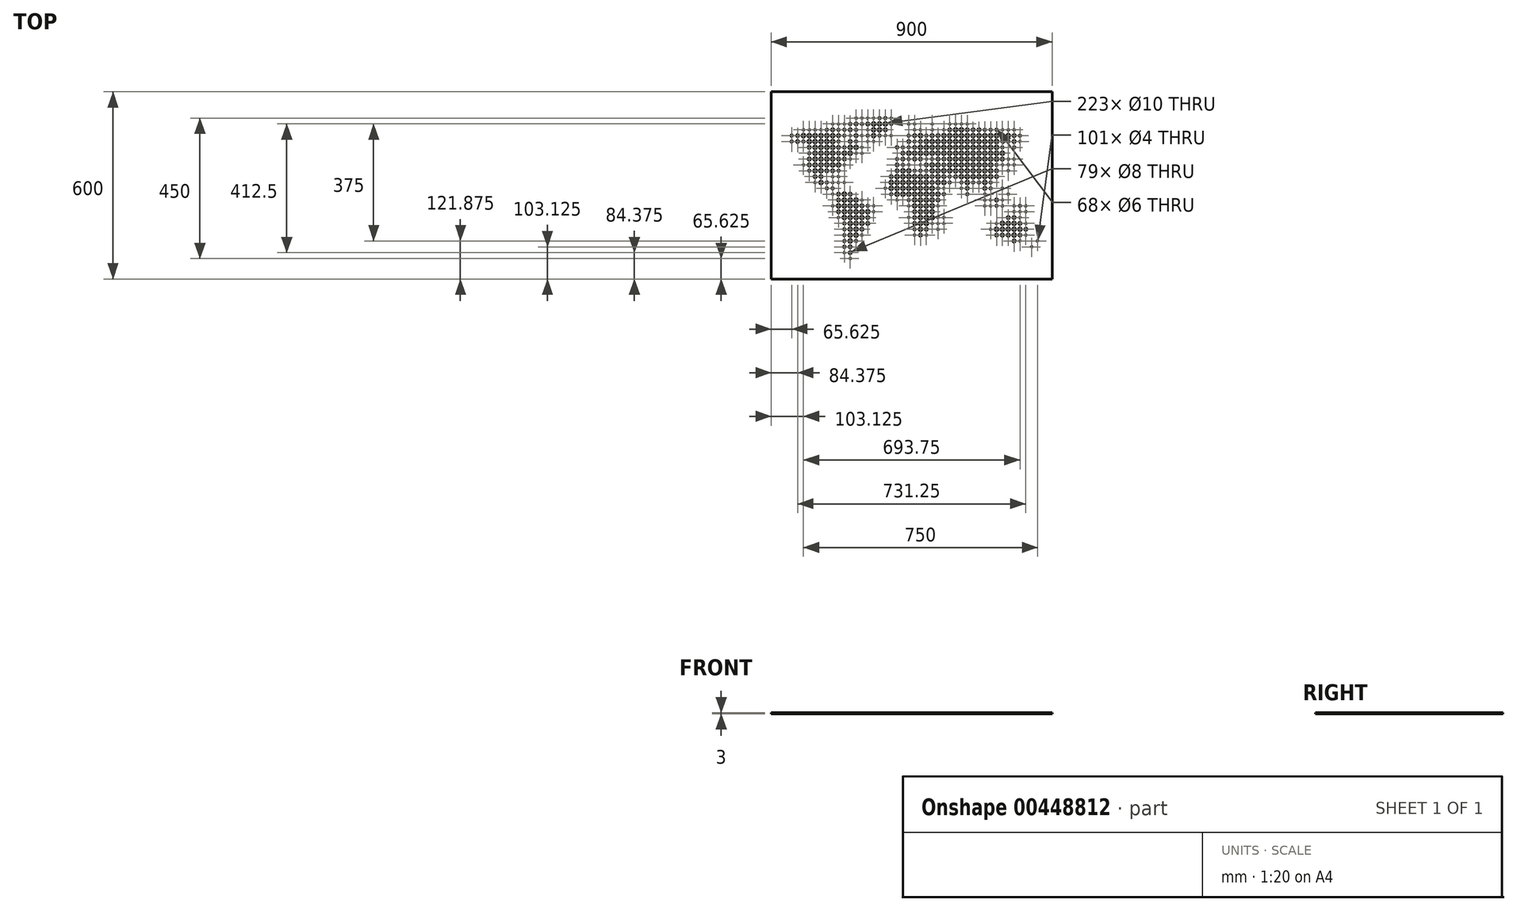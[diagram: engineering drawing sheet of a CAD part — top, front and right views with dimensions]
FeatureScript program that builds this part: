
annotation { "Feature Type Name" : "Feature", "Feature Type Description" : "" }
export const myFeature = defineFeature(function(context is Context, id is Id, definition is map)
    precondition{}
    {
        {
            var Q0;
            Q0=qCreatedBy(makeId("Top.planeOp"),FACE);
            var sketch = newSketch(context, id + "F0", { "sketchPlane" : qUnion([Q0])});
            skLineSegment(sketch, "E0.bottom", {"start": v(450, -300) * mm, "end": v(-450, -300) * mm});
            skLineSegment(sketch, "E0.top", {"start": v(450, 300) * mm, "end": v(-450, 300) * mm});
            skLineSegment(sketch, "E0.left", {"start": v(450, -300) * mm, "end": v(450, 300) * mm});
            skLineSegment(sketch, "E0.right", {"start": v(-450, -300) * mm, "end": v(-450, 300) * mm});
            skPoint(sketch, "E0.middle", {"position": v(0, 0) * mm});
            skSolve(sketch);
        }
        {
            var Q0;
            Q0=makeQuery(id+"F0.imprint","IMPRINT",FACE,{"disambiguationData":[TD([[makeQuery(id+"F0.imprint","IMPRINT",EDGE,{"derivedFrom":sQuery(id+"F0.wireOp",EDGE,"E0.bottom")}),-1.0]])]});
            extrude(context, id + "F1", {"entities" : qUnion([Q0]), "depth" : 3 * mm});
        }
        {
            var Q0;
            Q0=makeQuery(id+"F1.opExtrude","CAP_FACE",FACE,{"disambiguationData":[OSD([sQuery(id+"F0.wireOp",EDGE,"E0.bottom"),sQuery(id+"F0.wireOp",EDGE,"E0.top"),sQuery(id+"F0.wireOp",EDGE,"E0.left"),sQuery(id+"F0.wireOp",EDGE,"E0.right")])],"isStart":false});
            var sketch = newSketch(context, id + "F2", { "sketchPlane" : qUnion([Q0])});
            skLineSegment(sketch, "E1", {"start": v(-440.63, 300) * mm, "end": v(-440.62, -300) * mm, "construction": true});
            skLineSegment(sketch, "E2.1.0.0", {"start": v(-421.88, 300) * mm, "end": v(-421.88, -300) * mm, "construction": true});
            skLineSegment(sketch, "E2.2.0.0", {"start": v(-403.13, 300) * mm, "end": v(-403.13, -300) * mm, "construction": true});
            skLineSegment(sketch, "E2.3.0.0", {"start": v(-384.38, 300) * mm, "end": v(-384.38, -300) * mm, "construction": true});
            skLineSegment(sketch, "E2.4.0.0", {"start": v(-365.63, 300) * mm, "end": v(-365.63, -300) * mm, "construction": true});
            skLineSegment(sketch, "E2.5.0.0", {"start": v(-346.88, 300) * mm, "end": v(-346.88, -300) * mm, "construction": true});
            skLineSegment(sketch, "E2.6.0.0", {"start": v(-328.13, 300) * mm, "end": v(-328.13, -300) * mm, "construction": true});
            skLineSegment(sketch, "E2.7.0.0", {"start": v(-309.38, 300) * mm, "end": v(-309.38, -300) * mm, "construction": true});
            skLineSegment(sketch, "E2.8.0.0", {"start": v(-290.63, 300) * mm, "end": v(-290.63, -300) * mm, "construction": true});
            skLineSegment(sketch, "E2.9.0.0", {"start": v(-271.88, 300) * mm, "end": v(-271.88, -300) * mm, "construction": true});
            skLineSegment(sketch, "E2.direction1", {"start": v(-440.62, -300) * mm, "end": v(-421.88, -300) * mm, "construction": true});
            skLineSegment(sketch, "E3.0.10.0", {"start": v(-253.13, 300) * mm, "end": v(-253.13, -300) * mm, "construction": true});
            skLineSegment(sketch, "E3.0.11.0", {"start": v(-234.38, 300) * mm, "end": v(-234.38, -300) * mm, "construction": true});
            skLineSegment(sketch, "E3.0.12.0", {"start": v(-215.63, 300) * mm, "end": v(-215.63, -300) * mm, "construction": true});
            skLineSegment(sketch, "E3.0.13.0", {"start": v(-196.88, 300) * mm, "end": v(-196.88, -300) * mm, "construction": true});
            skLineSegment(sketch, "E3.0.14.0", {"start": v(-178.13, 300) * mm, "end": v(-178.13, -300) * mm, "construction": true});
            skLineSegment(sketch, "E3.0.15.0", {"start": v(-159.38, 300) * mm, "end": v(-159.38, -300) * mm, "construction": true});
            skLineSegment(sketch, "E3.0.16.0", {"start": v(-140.63, 300) * mm, "end": v(-140.63, -300) * mm, "construction": true});
            skLineSegment(sketch, "E3.0.17.0", {"start": v(-121.88, 300) * mm, "end": v(-121.88, -300) * mm, "construction": true});
            skLineSegment(sketch, "E3.0.18.0", {"start": v(-103.13, 300) * mm, "end": v(-103.13, -300) * mm, "construction": true});
            skLineSegment(sketch, "E3.0.19.0", {"start": v(-84.38, 300) * mm, "end": v(-84.38, -300) * mm, "construction": true});
            skLineSegment(sketch, "E4.0.20.0", {"start": v(-65.63, 300) * mm, "end": v(-65.63, -300) * mm, "construction": true});
            skLineSegment(sketch, "E4.0.21.0", {"start": v(-46.88, 300) * mm, "end": v(-46.88, -300) * mm, "construction": true});
            skLineSegment(sketch, "E4.0.22.0", {"start": v(-28.13, 300) * mm, "end": v(-28.13, -300) * mm, "construction": true});
            skLineSegment(sketch, "E4.0.23.0", {"start": v(-9.38, 300) * mm, "end": v(-9.38, -300) * mm, "construction": true});
            skLineSegment(sketch, "E4.0.24.0", {"start": v(9.37, 300) * mm, "end": v(9.37, -300) * mm, "construction": true});
            skLineSegment(sketch, "E4.0.25.0", {"start": v(28.12, 300) * mm, "end": v(28.12, -300) * mm, "construction": true});
            skLineSegment(sketch, "E4.0.26.0", {"start": v(46.87, 300) * mm, "end": v(46.87, -300) * mm, "construction": true});
            skLineSegment(sketch, "E4.0.27.0", {"start": v(65.62, 300) * mm, "end": v(65.62, -300) * mm, "construction": true});
            skLineSegment(sketch, "E4.0.28.0", {"start": v(84.37, 300) * mm, "end": v(84.37, -300) * mm, "construction": true});
            skLineSegment(sketch, "E4.0.29.0", {"start": v(103.12, 300) * mm, "end": v(103.12, -300) * mm, "construction": true});
            skLineSegment(sketch, "E5.0.30.0", {"start": v(121.87, 300) * mm, "end": v(121.87, -300) * mm, "construction": true});
            skLineSegment(sketch, "E5.0.31.0", {"start": v(140.62, 300) * mm, "end": v(140.62, -300) * mm, "construction": true});
            skLineSegment(sketch, "E5.0.32.0", {"start": v(159.37, 300) * mm, "end": v(159.37, -300) * mm, "construction": true});
            skLineSegment(sketch, "E5.0.33.0", {"start": v(178.12, 300) * mm, "end": v(178.12, -300) * mm, "construction": true});
            skLineSegment(sketch, "E5.0.34.0", {"start": v(196.87, 300) * mm, "end": v(196.87, -300) * mm, "construction": true});
            skLineSegment(sketch, "E5.0.35.0", {"start": v(215.62, 300) * mm, "end": v(215.62, -300) * mm, "construction": true});
            skLineSegment(sketch, "E5.0.36.0", {"start": v(234.37, 300) * mm, "end": v(234.37, -300) * mm, "construction": true});
            skLineSegment(sketch, "E5.0.37.0", {"start": v(253.12, 300) * mm, "end": v(253.12, -300) * mm, "construction": true});
            skLineSegment(sketch, "E5.0.38.0", {"start": v(271.87, 300) * mm, "end": v(271.87, -300) * mm, "construction": true});
            skLineSegment(sketch, "E5.0.39.0", {"start": v(290.62, 300) * mm, "end": v(290.62, -300) * mm, "construction": true});
            skLineSegment(sketch, "E5.0.40.0", {"start": v(309.37, 300) * mm, "end": v(309.37, -300) * mm, "construction": true});
            skLineSegment(sketch, "E5.0.41.0", {"start": v(328.12, 300) * mm, "end": v(328.12, -300) * mm, "construction": true});
            skLineSegment(sketch, "E5.0.42.0", {"start": v(346.87, 300) * mm, "end": v(346.87, -300) * mm, "construction": true});
            skLineSegment(sketch, "E5.0.43.0", {"start": v(365.62, 300) * mm, "end": v(365.62, -300) * mm, "construction": true});
            skLineSegment(sketch, "E5.0.44.0", {"start": v(384.37, 300) * mm, "end": v(384.37, -300) * mm, "construction": true});
            skLineSegment(sketch, "E5.0.45.0", {"start": v(403.12, 300) * mm, "end": v(403.12, -300) * mm, "construction": true});
            skLineSegment(sketch, "E5.0.46.0", {"start": v(421.87, 300) * mm, "end": v(421.87, -300) * mm, "construction": true});
            skLineSegment(sketch, "E5.0.47.0", {"start": v(440.62, 300) * mm, "end": v(440.62, -300) * mm, "construction": true});
            skLineSegment(sketch, "E6", {"start": v(-450, -290.63) * mm, "end": v(450, -290.63) * mm, "construction": true});
            skLineSegment(sketch, "E7.0.1.0", {"start": v(-450, -271.88) * mm, "end": v(450, -271.88) * mm, "construction": true});
            skLineSegment(sketch, "E7.0.2.0", {"start": v(-450, -253.13) * mm, "end": v(450, -253.13) * mm, "construction": true});
            skLineSegment(sketch, "E7.0.3.0", {"start": v(-450, -234.38) * mm, "end": v(450, -234.38) * mm, "construction": true});
            skLineSegment(sketch, "E7.0.4.0", {"start": v(-450, -215.63) * mm, "end": v(450, -215.63) * mm, "construction": true});
            skLineSegment(sketch, "E7.0.5.0", {"start": v(-450, -196.88) * mm, "end": v(450, -196.88) * mm, "construction": true});
            skLineSegment(sketch, "E7.0.6.0", {"start": v(-450, -178.13) * mm, "end": v(450, -178.13) * mm, "construction": true});
            skLineSegment(sketch, "E7.0.7.0", {"start": v(-450, -159.38) * mm, "end": v(450, -159.38) * mm, "construction": true});
            skLineSegment(sketch, "E7.0.8.0", {"start": v(-450, -140.63) * mm, "end": v(450, -140.63) * mm, "construction": true});
            skLineSegment(sketch, "E7.0.9.0", {"start": v(-450, -121.88) * mm, "end": v(450, -121.88) * mm, "construction": true});
            skLineSegment(sketch, "E7.direction1", {"start": v(-450, -290.63) * mm, "end": v(-425, -290.63) * mm, "construction": true});
            skLineSegment(sketch, "E7.direction2", {"start": v(-450, -290.63) * mm, "end": v(-450, -271.88) * mm, "construction": true});
            skLineSegment(sketch, "E8.0.0.10", {"start": v(-450, -103.13) * mm, "end": v(450, -103.13) * mm, "construction": true});
            skLineSegment(sketch, "E8.0.0.11", {"start": v(-450, -84.38) * mm, "end": v(450, -84.38) * mm, "construction": true});
            skLineSegment(sketch, "E8.0.0.12", {"start": v(-450, -65.63) * mm, "end": v(450, -65.63) * mm, "construction": true});
            skLineSegment(sketch, "E8.0.0.13", {"start": v(-450, -46.88) * mm, "end": v(450, -46.88) * mm, "construction": true});
            skLineSegment(sketch, "E8.0.0.14", {"start": v(-450, -28.13) * mm, "end": v(450, -28.13) * mm, "construction": true});
            skLineSegment(sketch, "E8.0.0.15", {"start": v(-450, -9.38) * mm, "end": v(450, -9.38) * mm, "construction": true});
            skLineSegment(sketch, "E8.0.0.16", {"start": v(-450, 9.37) * mm, "end": v(450, 9.37) * mm, "construction": true});
            skLineSegment(sketch, "E8.0.0.17", {"start": v(-450, 28.12) * mm, "end": v(450, 28.12) * mm, "construction": true});
            skLineSegment(sketch, "E8.0.0.18", {"start": v(-450, 46.87) * mm, "end": v(450, 46.87) * mm, "construction": true});
            skLineSegment(sketch, "E8.0.0.19", {"start": v(-450, 65.62) * mm, "end": v(450, 65.62) * mm, "construction": true});
            skLineSegment(sketch, "E9.0.0.20", {"start": v(-450, 84.37) * mm, "end": v(450, 84.37) * mm, "construction": true});
            skLineSegment(sketch, "E9.0.0.21", {"start": v(-450, 103.12) * mm, "end": v(450, 103.12) * mm, "construction": true});
            skLineSegment(sketch, "E9.0.0.22", {"start": v(-450, 121.87) * mm, "end": v(450, 121.87) * mm, "construction": true});
            skLineSegment(sketch, "E9.0.0.23", {"start": v(-450, 140.62) * mm, "end": v(450, 140.62) * mm, "construction": true});
            skLineSegment(sketch, "E9.0.0.24", {"start": v(-450, 159.37) * mm, "end": v(450, 159.37) * mm, "construction": true});
            skLineSegment(sketch, "E9.0.0.25", {"start": v(-450, 178.12) * mm, "end": v(450, 178.12) * mm, "construction": true});
            skLineSegment(sketch, "E9.0.0.26", {"start": v(-450, 196.87) * mm, "end": v(450, 196.87) * mm, "construction": true});
            skLineSegment(sketch, "E9.0.0.27", {"start": v(-450, 215.62) * mm, "end": v(450, 215.62) * mm, "construction": true});
            skLineSegment(sketch, "E9.0.0.28", {"start": v(-450, 234.37) * mm, "end": v(450, 234.37) * mm, "construction": true});
            skLineSegment(sketch, "E9.0.0.29", {"start": v(-450, 253.12) * mm, "end": v(450, 253.12) * mm, "construction": true});
            skLineSegment(sketch, "E10.0.0.30", {"start": v(-450, 271.87) * mm, "end": v(450, 271.87) * mm, "construction": true});
            skLineSegment(sketch, "E10.0.0.31", {"start": v(-450, 290.62) * mm, "end": v(450, 290.62) * mm, "construction": true});
            skSolve(sketch);
        }
        {
            var Q0;
            Q0=makeQuery(id+"F2.imprint","IMPRINT",FACE,{"disambiguationData":[TD([[makeQuery(id+"F2.imprint","IMPRINT",EDGE,{"derivedFrom":makeQuery(id+"F1.opExtrude","CAP_EDGE",EDGE,{"disambiguationData":[OSD([sQuery(id+"F0.wireOp",EDGE,"E0.bottom")])],"isStart":false})}),-1.0]])]});
            var sketch = newSketch(context, id + "F3", { "sketchPlane" : qUnion([Q0])});
            skPoint(sketch, "E11", {"position": v(-65.63, 215.62) * mm});
            skPoint(sketch, "E12", {"position": v(-121.88, 215.62) * mm});
            skPoint(sketch, "E13", {"position": v(-140.63, 215.62) * mm});
            skPoint(sketch, "E14", {"position": v(-159.38, 215.62) * mm});
            skPoint(sketch, "E15", {"position": v(-178.13, 215.62) * mm});
            skPoint(sketch, "E16", {"position": v(-215.63, 196.87) * mm});
            skPoint(sketch, "E17", {"position": v(-234.38, 196.87) * mm});
            skPoint(sketch, "E18", {"position": v(-253.13, 196.87) * mm});
            skPoint(sketch, "E19", {"position": v(-290.63, 178.12) * mm});
            skPoint(sketch, "E20", {"position": v(-309.38, 178.12) * mm});
            skPoint(sketch, "E21", {"position": v(-328.13, 178.12) * mm});
            skPoint(sketch, "E22", {"position": v(-346.88, 178.12) * mm});
            skPoint(sketch, "E23", {"position": v(-140.63, 178.12) * mm});
            skPoint(sketch, "E24", {"position": v(-65.63, 159.37) * mm});
            skPoint(sketch, "E25", {"position": v(-84.38, 159.37) * mm});
            skPoint(sketch, "E26", {"position": v(-140.63, 140.62) * mm});
            skPoint(sketch, "E27", {"position": v(-121.88, 140.62) * mm});
            skPoint(sketch, "E28", {"position": v(-159.38, 121.87) * mm});
            skPoint(sketch, "E29", {"position": v(-159.38, 103.12) * mm});
            skPoint(sketch, "E30", {"position": v(-178.13, 103.12) * mm});
            skPoint(sketch, "E31", {"position": v(-196.88, 84.37) * mm});
            skPoint(sketch, "E32", {"position": v(-215.63, 65.62) * mm});
            skPoint(sketch, "E33", {"position": v(-234.38, 28.12) * mm});
            skPoint(sketch, "E34", {"position": v(-253.13, 28.12) * mm});
            skPoint(sketch, "E35", {"position": v(-253.13, 9.37) * mm});
            skPoint(sketch, "E36", {"position": v(-234.38, 9.37) * mm});
            skPoint(sketch, "E37", {"position": v(-215.63, 9.37) * mm});
            skPoint(sketch, "E38", {"position": v(-309.38, 9.37) * mm});
            skPoint(sketch, "E39", {"position": v(-253.13, -28.13) * mm});
            skPoint(sketch, "E40", {"position": v(-253.13, -65.63) * mm});
            skPoint(sketch, "E41", {"position": v(-159.38, -46.88) * mm});
            skPoint(sketch, "E42", {"position": v(-121.88, -65.63) * mm});
            skPoint(sketch, "E43", {"position": v(-121.88, -84.38) * mm});
            skPoint(sketch, "E44", {"position": v(-234.38, -103.13) * mm});
            skPoint(sketch, "E45", {"position": v(-215.63, -215.63) * mm});
            skPoint(sketch, "E46", {"position": v(-196.88, -234.38) * mm});
            skPoint(sketch, "E47", {"position": v(-159.38, -159.38) * mm});
            skPoint(sketch, "E48", {"position": v(-9.38, 196.87) * mm});
            skPoint(sketch, "E49", {"position": v(9.37, 196.87) * mm});
            skPoint(sketch, "E50", {"position": v(9.37, 178.12) * mm});
            skPoint(sketch, "E51", {"position": v(28.12, 178.12) * mm});
            skPoint(sketch, "E52", {"position": v(65.62, 178.12) * mm});
            skPoint(sketch, "E53", {"position": v(65.62, 196.87) * mm});
            skPoint(sketch, "E54", {"position": v(103.12, 178.12) * mm});
            skPoint(sketch, "E55", {"position": v(121.87, 196.87) * mm});
            skPoint(sketch, "E56", {"position": v(140.62, 196.87) * mm});
            skPoint(sketch, "E57", {"position": v(159.37, 196.87) * mm});
            skPoint(sketch, "E58", {"position": v(178.12, 196.87) * mm});
            skPoint(sketch, "E59", {"position": v(290.62, 178.12) * mm});
            skPoint(sketch, "E60", {"position": v(309.37, 178.12) * mm});
            skPoint(sketch, "E61", {"position": v(328.12, 178.12) * mm});
            skPoint(sketch, "E62", {"position": v(46.87, 84.37) * mm});
            skPoint(sketch, "E63", {"position": v(28.12, 65.62) * mm});
            skPoint(sketch, "E64", {"position": v(-9.38, 65.62) * mm});
            skPoint(sketch, "E65", {"position": v(346.87, 140.62) * mm});
            skPoint(sketch, "E66", {"position": v(328.12, 84.37) * mm});
            skPoint(sketch, "E67", {"position": v(309.37, 84.37) * mm});
            skPoint(sketch, "E68", {"position": v(309.37, 65.62) * mm});
            skPoint(sketch, "E69", {"position": v(328.12, 65.62) * mm});
            skPoint(sketch, "E70", {"position": v(309.37, 46.87) * mm});
            skPoint(sketch, "E71", {"position": v(290.62, 65.62) * mm});
            skPoint(sketch, "E72", {"position": v(-84.38, -9.38) * mm});
            skPoint(sketch, "E73", {"position": v(-46.88, -46.88) * mm});
            skPoint(sketch, "E74", {"position": v(-9.38, -65.63) * mm});
            skPoint(sketch, "E75", {"position": v(-9.38, -103.13) * mm});
            skPoint(sketch, "E76", {"position": v(9.37, -159.38) * mm});
            skPoint(sketch, "E77", {"position": v(46.87, -159.38) * mm});
            skPoint(sketch, "E78", {"position": v(65.62, -121.88) * mm});
            skPoint(sketch, "E79", {"position": v(84.37, -121.88) * mm});
            skPoint(sketch, "E80", {"position": v(103.12, -121.88) * mm});
            skPoint(sketch, "E81", {"position": v(103.12, -103.13) * mm});
            skPoint(sketch, "E82", {"position": v(84.37, -103.13) * mm});
            skPoint(sketch, "E83", {"position": v(84.37, -140.63) * mm});
            skPoint(sketch, "E84", {"position": v(84.37, -65.63) * mm});
            skPoint(sketch, "E85", {"position": v(103.12, -9.38) * mm});
            skPoint(sketch, "E86", {"position": v(159.37, -9.38) * mm});
            skPoint(sketch, "E87", {"position": v(234.37, -28.13) * mm});
            skPoint(sketch, "E88", {"position": v(234.37, -46.88) * mm});
            skPoint(sketch, "E89", {"position": v(253.12, -46.88) * mm});
            skPoint(sketch, "E90", {"position": v(253.12, -65.63) * mm});
            skPoint(sketch, "E91", {"position": v(234.37, -65.63) * mm});
            skPoint(sketch, "E92", {"position": v(290.62, -46.88) * mm});
            skPoint(sketch, "E93", {"position": v(290.62, -65.63) * mm});
            skPoint(sketch, "E94", {"position": v(309.37, -28.13) * mm});
            skPoint(sketch, "E95", {"position": v(290.62, -9.38) * mm});
            skPoint(sketch, "E96", {"position": v(328.12, -65.63) * mm});
            skPoint(sketch, "E97", {"position": v(365.62, -65.63) * mm});
            skPoint(sketch, "E98", {"position": v(365.62, -84.38) * mm});
            skPoint(sketch, "E99", {"position": v(346.87, -84.38) * mm});
            skPoint(sketch, "E100", {"position": v(328.12, -84.38) * mm});
            skPoint(sketch, "E101", {"position": v(346.87, -103.13) * mm});
            skPoint(sketch, "E102", {"position": v(365.62, -121.88) * mm});
            skPoint(sketch, "E103", {"position": v(365.62, -159.38) * mm});
            skPoint(sketch, "E104", {"position": v(346.87, -178.13) * mm});
            skPoint(sketch, "E105", {"position": v(403.12, -178.13) * mm});
            skPoint(sketch, "E106", {"position": v(384.37, -196.88) * mm});
            skPoint(sketch, "E107", {"position": v(271.87, -121.88) * mm});
            skPoint(sketch, "E108", {"position": v(253.12, -140.63) * mm});
            skPoint(sketch, "E109", {"position": v(-346.88, 65.62) * mm});
            skPoint(sketch, "E110", {"position": v(-159.38, 159.37) * mm});
            skPoint(sketch, "E111", {"position": v(-196.88, 159.37) * mm});
            skSolve(sketch);
        }
        {
            var Q0;
            Q0=sQuery(id+"F3.wireOp",VERTEX,"E34");
            var Q1;
            Q1=sQuery(id+"F3.wireOp",VERTEX,"E11");
            var Q2;
            Q2=sQuery(id+"F3.wireOp",VERTEX,"E23");
            var Q3;
            Q3=sQuery(id+"F3.wireOp",VERTEX,"E25");
            var Q4;
            Q4=sQuery(id+"F3.wireOp",VERTEX,"E46");
            var Q5;
            Q5=sQuery(id+"F3.wireOp",VERTEX,"E32");
            var Q6;
            Q6=sQuery(id+"F3.wireOp",VERTEX,"E42");
            var Q7;
            Q7=sQuery(id+"F3.wireOp",VERTEX,"E35");
            var Q8;
            Q8=sQuery(id+"F3.wireOp",VERTEX,"E41");
            var Q9;
            Q9=sQuery(id+"F3.wireOp",VERTEX,"E19");
            var Q10;
            Q10=sQuery(id+"F3.wireOp",VERTEX,"E31");
            var Q11;
            Q11=sQuery(id+"F3.wireOp",VERTEX,"E36");
            var Q12;
            Q12=sQuery(id+"F3.wireOp",VERTEX,"E111");
            var Q13;
            Q13=sQuery(id+"F3.wireOp",VERTEX,"E12");
            var Q14;
            Q14=sQuery(id+"F3.wireOp",VERTEX,"E43");
            var Q15;
            Q15=sQuery(id+"F3.wireOp",VERTEX,"E48");
            var Q16;
            Q16=sQuery(id+"F3.wireOp",VERTEX,"E30");
            var Q17;
            Q17=sQuery(id+"F3.wireOp",VERTEX,"E27");
            var Q18;
            Q18=sQuery(id+"F3.wireOp",VERTEX,"E40");
            var Q19;
            Q19=sQuery(id+"F3.wireOp",VERTEX,"E14");
            var Q20;
            Q20=sQuery(id+"F3.wireOp",VERTEX,"E15");
            var Q21;
            Q21=sQuery(id+"F3.wireOp",VERTEX,"E21");
            var Q22;
            Q22=sQuery(id+"F3.wireOp",VERTEX,"E75");
            var Q23;
            Q23=sQuery(id+"F3.wireOp",VERTEX,"E45");
            var Q24;
            Q24=sQuery(id+"F3.wireOp",VERTEX,"E109");
            var Q25;
            Q25=sQuery(id+"F3.wireOp",VERTEX,"E37");
            var Q26;
            Q26=sQuery(id+"F3.wireOp",VERTEX,"E29");
            var Q27;
            Q27=sQuery(id+"F3.wireOp",VERTEX,"E73");
            var Q28;
            Q28=sQuery(id+"F3.wireOp",VERTEX,"E24");
            var Q29;
            Q29=sQuery(id+"F3.wireOp",VERTEX,"E38");
            var Q30;
            Q30=sQuery(id+"F3.wireOp",VERTEX,"E72");
            var Q31;
            Q31=sQuery(id+"F3.wireOp",VERTEX,"E20");
            var Q32;
            Q32=sQuery(id+"F3.wireOp",VERTEX,"E13");
            var Q33;
            Q33=sQuery(id+"F3.wireOp",VERTEX,"E47");
            var Q34;
            Q34=sQuery(id+"F3.wireOp",VERTEX,"E16");
            var Q35;
            Q35=sQuery(id+"F3.wireOp",VERTEX,"E18");
            var Q36;
            Q36=sQuery(id+"F3.wireOp",VERTEX,"E64");
            var Q37;
            Q37=sQuery(id+"F3.wireOp",VERTEX,"E17");
            var Q38;
            Q38=sQuery(id+"F3.wireOp",VERTEX,"E22");
            var Q39;
            Q39=sQuery(id+"F3.wireOp",VERTEX,"E44");
            var Q40;
            Q40=sQuery(id+"F3.wireOp",VERTEX,"E28");
            var Q41;
            Q41=sQuery(id+"F3.wireOp",VERTEX,"E26");
            var Q42;
            Q42=sQuery(id+"F3.wireOp",VERTEX,"E39");
            var Q43;
            Q43=sQuery(id+"F3.wireOp",VERTEX,"E110");
            var Q44;
            Q44=sQuery(id+"F3.wireOp",VERTEX,"E74");
            var Q45;
            Q45=sQuery(id+"F3.wireOp",VERTEX,"E33");
            var Q46;
            Q46=makeQuery(id+"F1.opExtrude","SWEPT_BODY",BODY,{"disambiguationData":[OSD([sQuery(id+"F0.wireOp",EDGE,"E0.bottom"),sQuery(id+"F0.wireOp",EDGE,"E0.top"),sQuery(id+"F0.wireOp",EDGE,"E0.left"),sQuery(id+"F0.wireOp",EDGE,"E0.right")])]});
            hole(context, id + "F4", {"style" : HoleStyle.SIMPLE, "endStyle" : HoleEndStyle.THROUGH, "holeDiameter" : 4 * mm, "isTappedThrough" : true, "tappedDepth" : 12 * mm, "tapClearance" : 3, "locations" : qUnion([Q0, Q1, Q2, Q3, Q4, Q5, Q6, Q7, Q8, Q9, Q10, Q11, Q12, Q13, Q14, Q15, Q16, Q17, Q18, Q19, Q20, Q21, Q22, Q23, Q24, Q25, Q26, Q27, Q28, Q29, Q30, Q31, Q32, Q33, Q34, Q35, Q36, Q37, Q38, Q39, Q40, Q41, Q42, Q43, Q44, Q45]), "scope" : qUnion([Q46])});
        }
        {
            var Q0;
            Q0=sQuery(id+"F3.wireOp",VERTEX,"E105");
            var Q1;
            Q1=sQuery(id+"F3.wireOp",VERTEX,"E94");
            var Q2;
            Q2=sQuery(id+"F3.wireOp",VERTEX,"E52");
            var Q3;
            Q3=sQuery(id+"F3.wireOp",VERTEX,"E62");
            var Q4;
            Q4=sQuery(id+"F3.wireOp",VERTEX,"E11");
            var Q5;
            Q5=sQuery(id+"F3.wireOp",VERTEX,"E68");
            var Q6;
            Q6=sQuery(id+"F3.wireOp",VERTEX,"E84");
            var Q7;
            Q7=sQuery(id+"F3.wireOp",VERTEX,"E85");
            var Q8;
            Q8=sQuery(id+"F3.wireOp",VERTEX,"E25");
            var Q9;
            Q9=sQuery(id+"F3.wireOp",VERTEX,"E56");
            var Q10;
            Q10=sQuery(id+"F3.wireOp",VERTEX,"E69");
            var Q11;
            Q11=sQuery(id+"F3.wireOp",VERTEX,"E87");
            var Q12;
            Q12=sQuery(id+"F3.wireOp",VERTEX,"E54");
            var Q13;
            Q13=sQuery(id+"F3.wireOp",VERTEX,"E86");
            var Q14;
            Q14=sQuery(id+"F3.wireOp",VERTEX,"E60");
            var Q15;
            Q15=sQuery(id+"F3.wireOp",VERTEX,"E53");
            var Q16;
            Q16=sQuery(id+"F3.wireOp",VERTEX,"E79");
            var Q17;
            Q17=sQuery(id+"F3.wireOp",VERTEX,"E101");
            var Q18;
            Q18=sQuery(id+"F3.wireOp",VERTEX,"E66");
            var Q19;
            Q19=sQuery(id+"F3.wireOp",VERTEX,"E102");
            var Q20;
            Q20=sQuery(id+"F3.wireOp",VERTEX,"E70");
            var Q21;
            Q21=sQuery(id+"F3.wireOp",VERTEX,"E59");
            var Q22;
            Q22=sQuery(id+"F3.wireOp",VERTEX,"E77");
            var Q23;
            Q23=sQuery(id+"F3.wireOp",VERTEX,"E58");
            var Q24;
            Q24=sQuery(id+"F3.wireOp",VERTEX,"E78");
            var Q25;
            Q25=sQuery(id+"F3.wireOp",VERTEX,"E71");
            var Q26;
            Q26=sQuery(id+"F3.wireOp",VERTEX,"E50");
            var Q27;
            Q27=sQuery(id+"F3.wireOp",VERTEX,"E48");
            var Q28;
            Q28=sQuery(id+"F3.wireOp",VERTEX,"E57");
            var Q29;
            Q29=sQuery(id+"F3.wireOp",VERTEX,"E67");
            var Q30;
            Q30=sQuery(id+"F3.wireOp",VERTEX,"E83");
            var Q31;
            Q31=sQuery(id+"F3.wireOp",VERTEX,"E61");
            var Q32;
            Q32=sQuery(id+"F3.wireOp",VERTEX,"E93");
            var Q33;
            Q33=sQuery(id+"F3.wireOp",VERTEX,"E82");
            var Q34;
            Q34=sQuery(id+"F3.wireOp",VERTEX,"E74");
            var Q35;
            Q35=sQuery(id+"F3.wireOp",VERTEX,"E97");
            var Q36;
            Q36=sQuery(id+"F3.wireOp",VERTEX,"E49");
            var Q37;
            Q37=sQuery(id+"F3.wireOp",VERTEX,"E96");
            var Q38;
            Q38=sQuery(id+"F3.wireOp",VERTEX,"E75");
            var Q39;
            Q39=sQuery(id+"F3.wireOp",VERTEX,"E107");
            var Q40;
            Q40=sQuery(id+"F3.wireOp",VERTEX,"E81");
            var Q41;
            Q41=sQuery(id+"F3.wireOp",VERTEX,"E73");
            var Q42;
            Q42=sQuery(id+"F3.wireOp",VERTEX,"E24");
            var Q43;
            Q43=sQuery(id+"F3.wireOp",VERTEX,"E65");
            var Q44;
            Q44=sQuery(id+"F3.wireOp",VERTEX,"E72");
            var Q45;
            Q45=sQuery(id+"F3.wireOp",VERTEX,"E98");
            var Q46;
            Q46=sQuery(id+"F3.wireOp",VERTEX,"E80");
            var Q47;
            Q47=sQuery(id+"F3.wireOp",VERTEX,"E104");
            var Q48;
            Q48=sQuery(id+"F3.wireOp",VERTEX,"E89");
            var Q49;
            Q49=sQuery(id+"F3.wireOp",VERTEX,"E106");
            var Q50;
            Q50=sQuery(id+"F3.wireOp",VERTEX,"E88");
            var Q51;
            Q51=sQuery(id+"F3.wireOp",VERTEX,"E91");
            var Q52;
            Q52=sQuery(id+"F3.wireOp",VERTEX,"E64");
            var Q53;
            Q53=sQuery(id+"F3.wireOp",VERTEX,"E63");
            var Q54;
            Q54=sQuery(id+"F3.wireOp",VERTEX,"E95");
            var Q55;
            Q55=sQuery(id+"F3.wireOp",VERTEX,"E108");
            var Q56;
            Q56=sQuery(id+"F3.wireOp",VERTEX,"E76");
            var Q57;
            Q57=sQuery(id+"F3.wireOp",VERTEX,"E99");
            var Q58;
            Q58=sQuery(id+"F3.wireOp",VERTEX,"E103");
            var Q59;
            Q59=sQuery(id+"F3.wireOp",VERTEX,"E51");
            var Q60;
            Q60=sQuery(id+"F3.wireOp",VERTEX,"E55");
            var Q61;
            Q61=sQuery(id+"F3.wireOp",VERTEX,"E100");
            var Q62;
            Q62=sQuery(id+"F3.wireOp",VERTEX,"E90");
            var Q63;
            Q63=sQuery(id+"F3.wireOp",VERTEX,"E92");
            var Q64;
            Q64=makeQuery(id+"F1.opExtrude","SWEPT_BODY",BODY,{"disambiguationData":[OSD([sQuery(id+"F0.wireOp",EDGE,"E0.bottom"),sQuery(id+"F0.wireOp",EDGE,"E0.top"),sQuery(id+"F0.wireOp",EDGE,"E0.left"),sQuery(id+"F0.wireOp",EDGE,"E0.right")])]});
            hole(context, id + "F5", {"style" : HoleStyle.SIMPLE, "endStyle" : HoleEndStyle.THROUGH, "holeDiameter" : 4 * mm, "isTappedThrough" : true, "tappedDepth" : 12 * mm, "tapClearance" : 3, "locations" : qUnion([Q0, Q1, Q2, Q3, Q4, Q5, Q6, Q7, Q8, Q9, Q10, Q11, Q12, Q13, Q14, Q15, Q16, Q17, Q18, Q19, Q20, Q21, Q22, Q23, Q24, Q25, Q26, Q27, Q28, Q29, Q30, Q31, Q32, Q33, Q34, Q35, Q36, Q37, Q38, Q39, Q40, Q41, Q42, Q43, Q44, Q45, Q46, Q47, Q48, Q49, Q50, Q51, Q52, Q53, Q54, Q55, Q56, Q57, Q58, Q59, Q60, Q61, Q62, Q63]), "scope" : qUnion([Q64])});
        }
        {
            var Q0;
            Q0=makeQuery(id+"F2.imprint","IMPRINT",FACE,{"disambiguationData":[TD([[makeQuery(id+"F2.imprint","IMPRINT",EDGE,{"derivedFrom":makeQuery(id+"F1.opExtrude","CAP_EDGE",EDGE,{"disambiguationData":[OSD([sQuery(id+"F0.wireOp",EDGE,"E0.bottom")])],"isStart":false})}),-1.0]])]});
            var sketch = newSketch(context, id + "F6", { "sketchPlane" : qUnion([Q0])});
            skPoint(sketch, "E112", {"position": v(-84.38, 215.62) * mm});
            skPoint(sketch, "E113", {"position": v(-103.13, 215.62) * mm});
            skPoint(sketch, "E114", {"position": v(-65.63, 196.87) * mm});
            skPoint(sketch, "E115", {"position": v(-103.13, 159.37) * mm});
            skPoint(sketch, "E116", {"position": v(-140.63, 159.37) * mm});
            skPoint(sketch, "E117", {"position": v(-178.13, 178.12) * mm});
            skPoint(sketch, "E118", {"position": v(-178.13, 140.62) * mm});
            skPoint(sketch, "E119", {"position": v(-159.38, 196.87) * mm});
            skPoint(sketch, "E120", {"position": v(-196.88, 196.87) * mm});
            skPoint(sketch, "E121", {"position": v(-215.63, 178.12) * mm});
            skPoint(sketch, "E122", {"position": v(-215.63, 159.37) * mm});
            skPoint(sketch, "E123", {"position": v(-234.38, 178.12) * mm});
            skPoint(sketch, "E124", {"position": v(-271.88, 178.12) * mm});
            skPoint(sketch, "E125", {"position": v(-234.38, 140.62) * mm});
            skPoint(sketch, "E126", {"position": v(-215.63, 121.87) * mm});
            skPoint(sketch, "E127", {"position": v(-234.38, 46.87) * mm});
            skPoint(sketch, "E128", {"position": v(-346.88, 140.62) * mm});
            skPoint(sketch, "E129", {"position": v(-384.38, 159.37) * mm});
            skPoint(sketch, "E130", {"position": v(-384.38, 140.62) * mm});
            skPoint(sketch, "E131", {"position": v(-328.13, 103.12) * mm});
            skPoint(sketch, "E132", {"position": v(-328.13, 46.87) * mm});
            skPoint(sketch, "E133", {"position": v(-253.13, -9.38) * mm});
            skPoint(sketch, "E134", {"position": v(-271.88, -9.38) * mm});
            skPoint(sketch, "E135", {"position": v(-271.88, 9.37) * mm});
            skPoint(sketch, "E136", {"position": v(-140.63, -65.63) * mm});
            skPoint(sketch, "E137", {"position": v(-215.63, -196.88) * mm});
            skPoint(sketch, "E138", {"position": v(-215.63, -178.13) * mm});
            skPoint(sketch, "E139", {"position": v(-215.63, -159.38) * mm});
            skPoint(sketch, "E140", {"position": v(-215.63, -140.63) * mm});
            skPoint(sketch, "E141", {"position": v(-215.63, -121.88) * mm});
            skPoint(sketch, "E142", {"position": v(46.87, 159.37) * mm});
            skPoint(sketch, "E143", {"position": v(-9.38, 159.37) * mm});
            skPoint(sketch, "E144", {"position": v(9.37, 140.62) * mm});
            skPoint(sketch, "E145", {"position": v(-9.38, 121.87) * mm});
            skPoint(sketch, "E146", {"position": v(-28.13, 121.87) * mm});
            skPoint(sketch, "E147", {"position": v(-46.88, 121.87) * mm});
            skPoint(sketch, "E148", {"position": v(-9.38, 84.37) * mm});
            skPoint(sketch, "E149", {"position": v(-28.13, 65.62) * mm});
            skPoint(sketch, "E150", {"position": v(-46.88, 84.37) * mm});
            skPoint(sketch, "E151", {"position": v(9.37, 46.87) * mm});
            skPoint(sketch, "E152", {"position": v(28.12, 46.87) * mm});
            skPoint(sketch, "E153", {"position": v(46.87, 46.87) * mm});
            skPoint(sketch, "E154", {"position": v(65.62, 84.37) * mm});
            skPoint(sketch, "E155", {"position": v(271.87, 178.12) * mm});
            skPoint(sketch, "E156", {"position": v(253.12, 178.12) * mm});
            skPoint(sketch, "E157", {"position": v(234.37, 178.12) * mm});
            skPoint(sketch, "E158", {"position": v(346.87, 159.37) * mm});
            skPoint(sketch, "E159", {"position": v(328.12, 121.87) * mm});
            skPoint(sketch, "E160", {"position": v(309.37, 140.62) * mm});
            skPoint(sketch, "E161", {"position": v(290.62, 140.62) * mm});
            skPoint(sketch, "E162", {"position": v(290.62, 121.87) * mm});
            skPoint(sketch, "E163", {"position": v(271.87, 65.62) * mm});
            skPoint(sketch, "E164", {"position": v(121.87, 28.12) * mm});
            skPoint(sketch, "E165", {"position": v(121.87, 9.37) * mm});
            skPoint(sketch, "E166", {"position": v(84.37, -9.38) * mm});
            skPoint(sketch, "E167", {"position": v(103.12, -28.13) * mm});
            skPoint(sketch, "E168", {"position": v(-65.63, -28.13) * mm});
            skPoint(sketch, "E169", {"position": v(-9.38, -46.88) * mm});
            skPoint(sketch, "E170", {"position": v(9.37, -140.63) * mm});
            skPoint(sketch, "E171", {"position": v(159.37, 9.37) * mm});
            skPoint(sketch, "E172", {"position": v(178.12, -28.13) * mm});
            skPoint(sketch, "E173", {"position": v(196.87, 9.37) * mm});
            skPoint(sketch, "E174", {"position": v(215.62, 9.37) * mm});
            skPoint(sketch, "E175", {"position": v(253.12, 9.37) * mm});
            skPoint(sketch, "E176", {"position": v(253.12, -9.38) * mm});
            skPoint(sketch, "E177", {"position": v(271.87, -65.63) * mm});
            skPoint(sketch, "E178", {"position": v(346.87, -65.63) * mm});
            skPoint(sketch, "E179", {"position": v(-178.13, -178.13) * mm});
            skSolve(sketch);
        }
        {
            var Q0;
            Q0=sQuery(id+"F6.wireOp",VERTEX,"E167");
            var Q1;
            Q1=sQuery(id+"F6.wireOp",VERTEX,"E144");
            var Q2;
            Q2=sQuery(id+"F6.wireOp",VERTEX,"E152");
            var Q3;
            Q3=sQuery(id+"F6.wireOp",VERTEX,"E173");
            var Q4;
            Q4=sQuery(id+"F6.wireOp",VERTEX,"E128");
            var Q5;
            Q5=sQuery(id+"F6.wireOp",VERTEX,"E162");
            var Q6;
            Q6=sQuery(id+"F6.wireOp",VERTEX,"E122");
            var Q7;
            Q7=sQuery(id+"F6.wireOp",VERTEX,"E176");
            var Q8;
            Q8=sQuery(id+"F6.wireOp",VERTEX,"E130");
            var Q9;
            Q9=sQuery(id+"F6.wireOp",VERTEX,"E139");
            var Q10;
            Q10=sQuery(id+"F6.wireOp",VERTEX,"E151");
            var Q11;
            Q11=sQuery(id+"F6.wireOp",VERTEX,"E120");
            var Q12;
            Q12=sQuery(id+"F6.wireOp",VERTEX,"E118");
            var Q13;
            Q13=sQuery(id+"F6.wireOp",VERTEX,"E121");
            var Q14;
            Q14=sQuery(id+"F6.wireOp",VERTEX,"E112");
            var Q15;
            Q15=sQuery(id+"F6.wireOp",VERTEX,"E155");
            var Q16;
            Q16=sQuery(id+"F6.wireOp",VERTEX,"E171");
            var Q17;
            Q17=sQuery(id+"F6.wireOp",VERTEX,"E157");
            var Q18;
            Q18=sQuery(id+"F6.wireOp",VERTEX,"E117");
            var Q19;
            Q19=sQuery(id+"F6.wireOp",VERTEX,"E141");
            var Q20;
            Q20=sQuery(id+"F6.wireOp",VERTEX,"E132");
            var Q21;
            Q21=sQuery(id+"F6.wireOp",VERTEX,"E148");
            var Q22;
            Q22=sQuery(id+"F6.wireOp",VERTEX,"E114");
            var Q23;
            Q23=sQuery(id+"F6.wireOp",VERTEX,"E168");
            var Q24;
            Q24=sQuery(id+"F6.wireOp",VERTEX,"E115");
            var Q25;
            Q25=sQuery(id+"F6.wireOp",VERTEX,"E178");
            var Q26;
            Q26=sQuery(id+"F6.wireOp",VERTEX,"E113");
            var Q27;
            Q27=sQuery(id+"F6.wireOp",VERTEX,"E164");
            var Q28;
            Q28=sQuery(id+"F6.wireOp",VERTEX,"E127");
            var Q29;
            Q29=sQuery(id+"F6.wireOp",VERTEX,"E142");
            var Q30;
            Q30=sQuery(id+"F6.wireOp",VERTEX,"E123");
            var Q31;
            Q31=sQuery(id+"F6.wireOp",VERTEX,"E138");
            var Q32;
            Q32=sQuery(id+"F6.wireOp",VERTEX,"E129");
            var Q33;
            Q33=sQuery(id+"F6.wireOp",VERTEX,"E154");
            var Q34;
            Q34=sQuery(id+"F6.wireOp",VERTEX,"E161");
            var Q35;
            Q35=sQuery(id+"F6.wireOp",VERTEX,"E145");
            var Q36;
            Q36=sQuery(id+"F6.wireOp",VERTEX,"E170");
            var Q37;
            Q37=sQuery(id+"F6.wireOp",VERTEX,"E172");
            var Q38;
            Q38=sQuery(id+"F6.wireOp",VERTEX,"E119");
            var Q39;
            Q39=sQuery(id+"F6.wireOp",VERTEX,"E147");
            var Q40;
            Q40=sQuery(id+"F6.wireOp",VERTEX,"E160");
            var Q41;
            Q41=sQuery(id+"F6.wireOp",VERTEX,"E131");
            var Q42;
            Q42=sQuery(id+"F6.wireOp",VERTEX,"E135");
            var Q43;
            Q43=sQuery(id+"F6.wireOp",VERTEX,"E163");
            var Q44;
            Q44=sQuery(id+"F6.wireOp",VERTEX,"E124");
            var Q45;
            Q45=sQuery(id+"F6.wireOp",VERTEX,"E169");
            var Q46;
            Q46=sQuery(id+"F6.wireOp",VERTEX,"E125");
            var Q47;
            Q47=sQuery(id+"F6.wireOp",VERTEX,"E153");
            var Q48;
            Q48=sQuery(id+"F6.wireOp",VERTEX,"E126");
            var Q49;
            Q49=sQuery(id+"F6.wireOp",VERTEX,"E137");
            var Q50;
            Q50=sQuery(id+"F6.wireOp",VERTEX,"E116");
            var Q51;
            Q51=sQuery(id+"F6.wireOp",VERTEX,"E146");
            var Q52;
            Q52=sQuery(id+"F6.wireOp",VERTEX,"E174");
            var Q53;
            Q53=sQuery(id+"F6.wireOp",VERTEX,"E150");
            var Q54;
            Q54=sQuery(id+"F6.wireOp",VERTEX,"E133");
            var Q55;
            Q55=sQuery(id+"F6.wireOp",VERTEX,"E143");
            var Q56;
            Q56=sQuery(id+"F6.wireOp",VERTEX,"E158");
            var Q57;
            Q57=sQuery(id+"F6.wireOp",VERTEX,"E166");
            var Q58;
            Q58=sQuery(id+"F6.wireOp",VERTEX,"E165");
            var Q59;
            Q59=sQuery(id+"F6.wireOp",VERTEX,"E159");
            var Q60;
            Q60=sQuery(id+"F6.wireOp",VERTEX,"E149");
            var Q61;
            Q61=sQuery(id+"F6.wireOp",VERTEX,"E134");
            var Q62;
            Q62=sQuery(id+"F6.wireOp",VERTEX,"E177");
            var Q63;
            Q63=sQuery(id+"F6.wireOp",VERTEX,"E175");
            var Q64;
            Q64=sQuery(id+"F6.wireOp",VERTEX,"E136");
            var Q65;
            Q65=sQuery(id+"F6.wireOp",VERTEX,"E140");
            var Q66;
            Q66=sQuery(id+"F6.wireOp",VERTEX,"E156");
            var Q67;
            Q67=sQuery(id+"F6.wireOp",VERTEX,"E179");
            var Q68;
            Q68=makeQuery(id+"F1.opExtrude","SWEPT_BODY",BODY,{"disambiguationData":[OSD([sQuery(id+"F0.wireOp",EDGE,"E0.bottom"),sQuery(id+"F0.wireOp",EDGE,"E0.top"),sQuery(id+"F0.wireOp",EDGE,"E0.left"),sQuery(id+"F0.wireOp",EDGE,"E0.right")])]});
            hole(context, id + "F7", {"style" : HoleStyle.SIMPLE, "endStyle" : HoleEndStyle.THROUGH, "holeDiameter" : 6 * mm, "isTappedThrough" : true, "tappedDepth" : 12 * mm, "tapClearance" : 3, "locations" : qUnion([Q0, Q1, Q2, Q3, Q4, Q5, Q6, Q7, Q8, Q9, Q10, Q11, Q12, Q13, Q14, Q15, Q16, Q17, Q18, Q19, Q20, Q21, Q22, Q23, Q24, Q25, Q26, Q27, Q28, Q29, Q30, Q31, Q32, Q33, Q34, Q35, Q36, Q37, Q38, Q39, Q40, Q41, Q42, Q43, Q44, Q45, Q46, Q47, Q48, Q49, Q50, Q51, Q52, Q53, Q54, Q55, Q56, Q57, Q58, Q59, Q60, Q61, Q62, Q63, Q64, Q65, Q66, Q67]), "scope" : qUnion([Q68])});
        }
        {
            var Q0;
            Q0=makeQuery(id+"F2.imprint","IMPRINT",FACE,{"disambiguationData":[TD([[makeQuery(id+"F2.imprint","IMPRINT",EDGE,{"derivedFrom":makeQuery(id+"F1.opExtrude","CAP_EDGE",EDGE,{"disambiguationData":[OSD([sQuery(id+"F0.wireOp",EDGE,"E0.bottom")])],"isStart":false})}),-1.0]])]});
            var sketch = newSketch(context, id + "F8", { "sketchPlane" : qUnion([Q0])});
            skPoint(sketch, "E180", {"position": v(-178.13, 196.87) * mm});
            skPoint(sketch, "E181", {"position": v(-140.63, 196.87) * mm});
            skPoint(sketch, "E182", {"position": v(-196.88, 178.12) * mm});
            skPoint(sketch, "E183", {"position": v(-178.13, 159.37) * mm});
            skPoint(sketch, "E184", {"position": v(-196.88, 140.62) * mm});
            skPoint(sketch, "E185", {"position": v(-84.38, 178.12) * mm});
            skPoint(sketch, "E186", {"position": v(-253.13, 178.12) * mm});
            skPoint(sketch, "E187", {"position": v(-234.38, 159.37) * mm});
            skPoint(sketch, "E188", {"position": v(-234.38, 121.87) * mm});
            skPoint(sketch, "E189", {"position": v(-234.38, 103.12) * mm});
            skPoint(sketch, "E190", {"position": v(-234.38, 84.37) * mm});
            skPoint(sketch, "E191", {"position": v(-215.63, 84.37) * mm});
            skPoint(sketch, "E192", {"position": v(-365.63, 159.37) * mm});
            skPoint(sketch, "E193", {"position": v(-365.63, 140.62) * mm});
            skPoint(sketch, "E194", {"position": v(-328.13, 121.87) * mm});
            skPoint(sketch, "E195", {"position": v(-328.13, 84.37) * mm});
            skPoint(sketch, "E196", {"position": v(-328.13, 65.62) * mm});
            skPoint(sketch, "E197", {"position": v(-309.38, 28.12) * mm});
            skPoint(sketch, "E198", {"position": v(-290.63, 28.12) * mm});
            skPoint(sketch, "E199", {"position": v(-271.88, 46.87) * mm});
            skPoint(sketch, "E200", {"position": v(-253.13, 46.87) * mm});
            skPoint(sketch, "E201", {"position": v(-234.38, -28.13) * mm});
            skPoint(sketch, "E202", {"position": v(-234.38, -46.88) * mm});
            skPoint(sketch, "E203", {"position": v(-196.88, -28.13) * mm});
            skPoint(sketch, "E204", {"position": v(-234.38, -84.38) * mm});
            skPoint(sketch, "E205", {"position": v(-159.38, -65.63) * mm});
            skPoint(sketch, "E206", {"position": v(-140.63, -103.13) * mm});
            skPoint(sketch, "E207", {"position": v(-140.63, -121.88) * mm});
            skPoint(sketch, "E208", {"position": v(-159.38, -140.63) * mm});
            skPoint(sketch, "E209", {"position": v(-196.88, -215.63) * mm});
            skPoint(sketch, "E210", {"position": v(-196.88, -196.88) * mm});
            skPoint(sketch, "E211", {"position": v(9.37, 159.37) * mm});
            skPoint(sketch, "E212", {"position": v(-9.38, 140.62) * mm});
            skPoint(sketch, "E213", {"position": v(28.12, 140.62) * mm});
            skPoint(sketch, "E214", {"position": v(9.37, 121.87) * mm});
            skPoint(sketch, "E215", {"position": v(-28.13, 103.12) * mm});
            skPoint(sketch, "E216", {"position": v(-28.13, 84.37) * mm});
            skPoint(sketch, "E217", {"position": v(-46.88, 65.62) * mm});
            skPoint(sketch, "E218", {"position": v(-46.88, 46.87) * mm});
            skPoint(sketch, "E219", {"position": v(-65.63, 28.12) * mm});
            skPoint(sketch, "E220", {"position": v(9.37, 84.37) * mm});
            skPoint(sketch, "E221", {"position": v(28.12, 84.37) * mm});
            skPoint(sketch, "E222", {"position": v(46.87, 65.62) * mm});
            skPoint(sketch, "E223", {"position": v(65.62, 159.37) * mm});
            skPoint(sketch, "E224", {"position": v(84.37, 159.37) * mm});
            skPoint(sketch, "E225", {"position": v(121.87, 178.12) * mm});
            skPoint(sketch, "E226", {"position": v(178.12, 178.12) * mm});
            skPoint(sketch, "E227", {"position": v(196.87, 178.12) * mm});
            skPoint(sketch, "E228", {"position": v(215.62, 178.12) * mm});
            skPoint(sketch, "E229", {"position": v(84.37, 84.37) * mm});
            skPoint(sketch, "E230", {"position": v(103.12, 84.37) * mm});
            skPoint(sketch, "E231", {"position": v(103.12, 65.62) * mm});
            skPoint(sketch, "E232", {"position": v(103.12, 28.12) * mm});
            skPoint(sketch, "E233", {"position": v(65.62, 28.12) * mm});
            skPoint(sketch, "E234", {"position": v(65.62, 9.37) * mm});
            skPoint(sketch, "E235", {"position": v(84.37, -46.88) * mm});
            skPoint(sketch, "E236", {"position": v(9.37, -103.13) * mm});
            skPoint(sketch, "E237", {"position": v(9.37, -84.38) * mm});
            skPoint(sketch, "E238", {"position": v(9.37, -121.88) * mm});
            skPoint(sketch, "E239", {"position": v(28.12, -159.38) * mm});
            skPoint(sketch, "E240", {"position": v(46.87, -140.63) * mm});
            skPoint(sketch, "E241", {"position": v(140.62, 28.12) * mm});
            skPoint(sketch, "E242", {"position": v(178.12, -9.38) * mm});
            skPoint(sketch, "E243", {"position": v(234.37, -9.38) * mm});
            skPoint(sketch, "E244", {"position": v(271.87, 28.12) * mm});
            skPoint(sketch, "E245", {"position": v(271.87, 46.87) * mm});
            skPoint(sketch, "E246", {"position": v(271.87, -46.88) * mm});
            skPoint(sketch, "E247", {"position": v(328.12, -103.13) * mm});
            skPoint(sketch, "E248", {"position": v(309.37, -103.13) * mm});
            skPoint(sketch, "E249", {"position": v(271.87, -159.38) * mm});
            skPoint(sketch, "E250", {"position": v(290.62, -159.38) * mm});
            skPoint(sketch, "E251", {"position": v(309.37, -159.38) * mm});
            skPoint(sketch, "E252", {"position": v(328.12, -178.13) * mm});
            skPoint(sketch, "E253", {"position": v(346.87, -159.38) * mm});
            skPoint(sketch, "E254", {"position": v(365.62, -140.63) * mm});
            skPoint(sketch, "E255", {"position": v(346.87, -121.88) * mm});
            skPoint(sketch, "E256", {"position": v(290.62, 84.37) * mm});
            skPoint(sketch, "E257", {"position": v(328.12, 140.62) * mm});
            skPoint(sketch, "E258", {"position": v(328.12, 159.37) * mm});
            skSolve(sketch);
        }
        {
            var Q0;
            Q0=sQuery(id+"F8.wireOp",VERTEX,"E200");
            var Q1;
            Q1=sQuery(id+"F8.wireOp",VERTEX,"E212");
            var Q2;
            Q2=sQuery(id+"F8.wireOp",VERTEX,"E192");
            var Q3;
            Q3=sQuery(id+"F8.wireOp",VERTEX,"E236");
            var Q4;
            Q4=sQuery(id+"F8.wireOp",VERTEX,"E191");
            var Q5;
            Q5=sQuery(id+"F8.wireOp",VERTEX,"E225");
            var Q6;
            Q6=sQuery(id+"F8.wireOp",VERTEX,"E243");
            var Q7;
            Q7=sQuery(id+"F8.wireOp",VERTEX,"E238");
            var Q8;
            Q8=sQuery(id+"F8.wireOp",VERTEX,"E228");
            var Q9;
            Q9=sQuery(id+"F8.wireOp",VERTEX,"E214");
            var Q10;
            Q10=sQuery(id+"F8.wireOp",VERTEX,"E250");
            var Q11;
            Q11=sQuery(id+"F8.wireOp",VERTEX,"E239");
            var Q12;
            Q12=sQuery(id+"F8.wireOp",VERTEX,"E220");
            var Q13;
            Q13=sQuery(id+"F8.wireOp",VERTEX,"E232");
            var Q14;
            Q14=sQuery(id+"F8.wireOp",VERTEX,"E252");
            var Q15;
            Q15=sQuery(id+"F8.wireOp",VERTEX,"E209");
            var Q16;
            Q16=sQuery(id+"F8.wireOp",VERTEX,"E241");
            var Q17;
            Q17=sQuery(id+"F8.wireOp",VERTEX,"E216");
            var Q18;
            Q18=sQuery(id+"F8.wireOp",VERTEX,"E196");
            var Q19;
            Q19=sQuery(id+"F8.wireOp",VERTEX,"E202");
            var Q20;
            Q20=sQuery(id+"F8.wireOp",VERTEX,"E180");
            var Q21;
            Q21=sQuery(id+"F8.wireOp",VERTEX,"E227");
            var Q22;
            Q22=sQuery(id+"F8.wireOp",VERTEX,"E189");
            var Q23;
            Q23=sQuery(id+"F8.wireOp",VERTEX,"E234");
            var Q24;
            Q24=sQuery(id+"F8.wireOp",VERTEX,"E255");
            var Q25;
            Q25=sQuery(id+"F8.wireOp",VERTEX,"E218");
            var Q26;
            Q26=sQuery(id+"F8.wireOp",VERTEX,"E242");
            var Q27;
            Q27=sQuery(id+"F8.wireOp",VERTEX,"E258");
            var Q28;
            Q28=sQuery(id+"F8.wireOp",VERTEX,"E211");
            var Q29;
            Q29=sQuery(id+"F8.wireOp",VERTEX,"E244");
            var Q30;
            Q30=sQuery(id+"F8.wireOp",VERTEX,"E184");
            var Q31;
            Q31=sQuery(id+"F8.wireOp",VERTEX,"E249");
            var Q32;
            Q32=sQuery(id+"F8.wireOp",VERTEX,"E186");
            var Q33;
            Q33=sQuery(id+"F8.wireOp",VERTEX,"E223");
            var Q34;
            Q34=sQuery(id+"F8.wireOp",VERTEX,"E183");
            var Q35;
            Q35=sQuery(id+"F8.wireOp",VERTEX,"E217");
            var Q36;
            Q36=sQuery(id+"F8.wireOp",VERTEX,"E188");
            var Q37;
            Q37=sQuery(id+"F8.wireOp",VERTEX,"E201");
            var Q38;
            Q38=sQuery(id+"F8.wireOp",VERTEX,"E219");
            var Q39;
            Q39=sQuery(id+"F8.wireOp",VERTEX,"E210");
            var Q40;
            Q40=sQuery(id+"F8.wireOp",VERTEX,"E185");
            var Q41;
            Q41=sQuery(id+"F8.wireOp",VERTEX,"E215");
            var Q42;
            Q42=sQuery(id+"F8.wireOp",VERTEX,"E187");
            var Q43;
            Q43=sQuery(id+"F8.wireOp",VERTEX,"E247");
            var Q44;
            Q44=sQuery(id+"F8.wireOp",VERTEX,"E251");
            var Q45;
            Q45=sQuery(id+"F8.wireOp",VERTEX,"E199");
            var Q46;
            Q46=sQuery(id+"F8.wireOp",VERTEX,"E182");
            var Q47;
            Q47=sQuery(id+"F8.wireOp",VERTEX,"E245");
            var Q48;
            Q48=sQuery(id+"F8.wireOp",VERTEX,"E205");
            var Q49;
            Q49=sQuery(id+"F8.wireOp",VERTEX,"E229");
            var Q50;
            Q50=sQuery(id+"F8.wireOp",VERTEX,"E237");
            var Q51;
            Q51=sQuery(id+"F8.wireOp",VERTEX,"E213");
            var Q52;
            Q52=sQuery(id+"F8.wireOp",VERTEX,"E206");
            var Q53;
            Q53=sQuery(id+"F8.wireOp",VERTEX,"E197");
            var Q54;
            Q54=sQuery(id+"F8.wireOp",VERTEX,"E208");
            var Q55;
            Q55=sQuery(id+"F8.wireOp",VERTEX,"E256");
            var Q56;
            Q56=sQuery(id+"F8.wireOp",VERTEX,"E231");
            var Q57;
            Q57=sQuery(id+"F8.wireOp",VERTEX,"E224");
            var Q58;
            Q58=sQuery(id+"F8.wireOp",VERTEX,"E190");
            var Q59;
            Q59=sQuery(id+"F8.wireOp",VERTEX,"E240");
            var Q60;
            Q60=sQuery(id+"F8.wireOp",VERTEX,"E226");
            var Q61;
            Q61=sQuery(id+"F8.wireOp",VERTEX,"E253");
            var Q62;
            Q62=sQuery(id+"F8.wireOp",VERTEX,"E233");
            var Q63;
            Q63=sQuery(id+"F8.wireOp",VERTEX,"E181");
            var Q64;
            Q64=sQuery(id+"F8.wireOp",VERTEX,"E222");
            var Q65;
            Q65=sQuery(id+"F8.wireOp",VERTEX,"E221");
            var Q66;
            Q66=sQuery(id+"F8.wireOp",VERTEX,"E254");
            var Q67;
            Q67=sQuery(id+"F8.wireOp",VERTEX,"E235");
            var Q68;
            Q68=sQuery(id+"F8.wireOp",VERTEX,"E204");
            var Q69;
            Q69=sQuery(id+"F8.wireOp",VERTEX,"E194");
            var Q70;
            Q70=sQuery(id+"F8.wireOp",VERTEX,"E207");
            var Q71;
            Q71=sQuery(id+"F8.wireOp",VERTEX,"E203");
            var Q72;
            Q72=sQuery(id+"F8.wireOp",VERTEX,"E246");
            var Q73;
            Q73=sQuery(id+"F8.wireOp",VERTEX,"E195");
            var Q74;
            Q74=sQuery(id+"F8.wireOp",VERTEX,"E257");
            var Q75;
            Q75=sQuery(id+"F8.wireOp",VERTEX,"E193");
            var Q76;
            Q76=sQuery(id+"F8.wireOp",VERTEX,"E248");
            var Q77;
            Q77=sQuery(id+"F8.wireOp",VERTEX,"E198");
            var Q78;
            Q78=sQuery(id+"F8.wireOp",VERTEX,"E230");
            var Q79;
            Q79=makeQuery(id+"F1.opExtrude","SWEPT_BODY",BODY,{"disambiguationData":[OSD([sQuery(id+"F0.wireOp",EDGE,"E0.bottom"),sQuery(id+"F0.wireOp",EDGE,"E0.top"),sQuery(id+"F0.wireOp",EDGE,"E0.left"),sQuery(id+"F0.wireOp",EDGE,"E0.right")])]});
            hole(context, id + "F9", {"style" : HoleStyle.SIMPLE, "endStyle" : HoleEndStyle.THROUGH, "holeDiameter" : 8 * mm, "isTappedThrough" : true, "tappedDepth" : 12 * mm, "tapClearance" : 3, "locations" : qUnion([Q0, Q1, Q2, Q3, Q4, Q5, Q6, Q7, Q8, Q9, Q10, Q11, Q12, Q13, Q14, Q15, Q16, Q17, Q18, Q19, Q20, Q21, Q22, Q23, Q24, Q25, Q26, Q27, Q28, Q29, Q30, Q31, Q32, Q33, Q34, Q35, Q36, Q37, Q38, Q39, Q40, Q41, Q42, Q43, Q44, Q45, Q46, Q47, Q48, Q49, Q50, Q51, Q52, Q53, Q54, Q55, Q56, Q57, Q58, Q59, Q60, Q61, Q62, Q63, Q64, Q65, Q66, Q67, Q68, Q69, Q70, Q71, Q72, Q73, Q74, Q75, Q76, Q77, Q78]), "scope" : qUnion([Q79])});
        }
        {
            var Q0;
            Q0=makeQuery(id+"F2.imprint","IMPRINT",FACE,{"disambiguationData":[TD([[makeQuery(id+"F2.imprint","IMPRINT",EDGE,{"derivedFrom":makeQuery(id+"F1.opExtrude","CAP_EDGE",EDGE,{"disambiguationData":[OSD([sQuery(id+"F0.wireOp",EDGE,"E0.bottom")])],"isStart":false})}),-1.0]])]});
            var sketch = newSketch(context, id + "F10", { "sketchPlane" : qUnion([Q0])});
            skPoint(sketch, "E259", {"position": v(-84.38, 196.87) * mm});
            skPoint(sketch, "E260", {"position": v(-103.13, 196.87) * mm});
            skPoint(sketch, "E261", {"position": v(-121.88, 196.87) * mm});
            skPoint(sketch, "E262", {"position": v(-121.88, 178.12) * mm});
            skPoint(sketch, "E263", {"position": v(-103.13, 178.12) * mm});
            skPoint(sketch, "E264", {"position": v(-121.88, 159.37) * mm});
            skPoint(sketch, "E265", {"position": v(-178.13, 121.87) * mm});
            skPoint(sketch, "E266", {"position": v(-196.88, 121.87) * mm});
            skPoint(sketch, "E267", {"position": v(-196.88, 103.12) * mm});
            skPoint(sketch, "E268", {"position": v(-215.63, 103.12) * mm});
            skPoint(sketch, "E269", {"position": v(-290.63, 9.37) * mm});
            skPoint(sketch, "E270", {"position": v(-290.63, 46.87) * mm});
            skPoint(sketch, "E271", {"position": v(-309.38, 46.87) * mm});
            skPoint(sketch, "E272", {"position": v(-309.38, 65.62) * mm});
            skPoint(sketch, "E273", {"position": v(-290.63, 65.62) * mm});
            skPoint(sketch, "E274", {"position": v(-271.88, 65.62) * mm});
            skPoint(sketch, "E275", {"position": v(-253.13, 65.62) * mm});
            skPoint(sketch, "E276", {"position": v(-234.38, 65.62) * mm});
            skPoint(sketch, "E277", {"position": v(-309.38, 84.37) * mm});
            skPoint(sketch, "E278", {"position": v(-309.38, 103.12) * mm});
            skPoint(sketch, "E279", {"position": v(-309.38, 121.87) * mm});
            skPoint(sketch, "E280", {"position": v(-309.38, 140.62) * mm});
            skPoint(sketch, "E281", {"position": v(-309.38, 159.37) * mm});
            skPoint(sketch, "E282", {"position": v(-328.13, 159.37) * mm});
            skPoint(sketch, "E283", {"position": v(-346.88, 159.37) * mm});
            skPoint(sketch, "E284", {"position": v(-328.13, 140.62) * mm});
            skPoint(sketch, "E285", {"position": v(-290.63, 159.37) * mm});
            skPoint(sketch, "E286", {"position": v(-271.88, 159.37) * mm});
            skPoint(sketch, "E287", {"position": v(-253.13, 159.37) * mm});
            skPoint(sketch, "E288", {"position": v(-253.13, 140.62) * mm});
            skPoint(sketch, "E289", {"position": v(-253.13, 121.87) * mm});
            skPoint(sketch, "E290", {"position": v(-253.13, 103.12) * mm});
            skPoint(sketch, "E291", {"position": v(-253.13, 84.37) * mm});
            skPoint(sketch, "E292", {"position": v(-271.88, 84.37) * mm});
            skPoint(sketch, "E293", {"position": v(-290.63, 84.37) * mm});
            skPoint(sketch, "E294", {"position": v(-290.63, 103.12) * mm});
            skPoint(sketch, "E295", {"position": v(-271.88, 103.12) * mm});
            skPoint(sketch, "E296", {"position": v(-271.88, 121.87) * mm});
            skPoint(sketch, "E297", {"position": v(-290.63, 121.87) * mm});
            skPoint(sketch, "E298", {"position": v(-290.63, 140.62) * mm});
            skPoint(sketch, "E299", {"position": v(-271.88, 140.62) * mm});
            skPoint(sketch, "E300", {"position": v(-215.63, -28.13) * mm});
            skPoint(sketch, "E301", {"position": v(-215.63, -46.88) * mm});
            skPoint(sketch, "E302", {"position": v(-196.88, -46.88) * mm});
            skPoint(sketch, "E303", {"position": v(-178.13, -46.88) * mm});
            skPoint(sketch, "E304", {"position": v(-234.38, -65.63) * mm});
            skPoint(sketch, "E305", {"position": v(-215.63, -65.63) * mm});
            skPoint(sketch, "E306", {"position": v(-196.88, -65.63) * mm});
            skPoint(sketch, "E307", {"position": v(-178.13, -65.63) * mm});
            skPoint(sketch, "E308", {"position": v(-215.63, -84.38) * mm});
            skPoint(sketch, "E309", {"position": v(-215.63, -103.13) * mm});
            skPoint(sketch, "E310", {"position": v(-196.88, -178.13) * mm});
            skPoint(sketch, "E311", {"position": v(-196.88, -159.38) * mm});
            skPoint(sketch, "E312", {"position": v(-196.88, -140.63) * mm});
            skPoint(sketch, "E313", {"position": v(-196.88, -121.88) * mm});
            skPoint(sketch, "E314", {"position": v(-196.88, -103.13) * mm});
            skPoint(sketch, "E315", {"position": v(-196.88, -84.38) * mm});
            skPoint(sketch, "E316", {"position": v(-178.13, -84.38) * mm});
            skPoint(sketch, "E317", {"position": v(-159.38, -84.38) * mm});
            skPoint(sketch, "E318", {"position": v(-140.63, -84.38) * mm});
            skPoint(sketch, "E319", {"position": v(-159.38, -103.13) * mm});
            skPoint(sketch, "E320", {"position": v(-159.38, -121.88) * mm});
            skPoint(sketch, "E321", {"position": v(-178.13, -121.88) * mm});
            skPoint(sketch, "E322", {"position": v(-178.13, -103.13) * mm});
            skPoint(sketch, "E323", {"position": v(-178.13, -159.38) * mm});
            skPoint(sketch, "E324", {"position": v(-178.13, -140.63) * mm});
            skPoint(sketch, "E325", {"position": v(28.12, 159.37) * mm});
            skPoint(sketch, "E326", {"position": v(103.12, 159.37) * mm});
            skPoint(sketch, "E327", {"position": v(121.87, 159.37) * mm});
            skPoint(sketch, "E328", {"position": v(140.62, 159.37) * mm});
            skPoint(sketch, "E329", {"position": v(159.37, 159.37) * mm});
            skPoint(sketch, "E330", {"position": v(178.12, 159.37) * mm});
            skPoint(sketch, "E331", {"position": v(196.87, 159.37) * mm});
            skPoint(sketch, "E332", {"position": v(215.62, 159.37) * mm});
            skPoint(sketch, "E333", {"position": v(234.37, 159.37) * mm});
            skPoint(sketch, "E334", {"position": v(253.12, 159.37) * mm});
            skPoint(sketch, "E335", {"position": v(271.87, 159.37) * mm});
            skPoint(sketch, "E336", {"position": v(290.62, 159.37) * mm});
            skPoint(sketch, "E337", {"position": v(309.37, 159.37) * mm});
            skPoint(sketch, "E338", {"position": v(140.62, 178.12) * mm});
            skPoint(sketch, "E339", {"position": v(159.37, 178.12) * mm});
            skPoint(sketch, "E340", {"position": v(46.87, 140.62) * mm});
            skPoint(sketch, "E341", {"position": v(65.62, 140.62) * mm});
            skPoint(sketch, "E342", {"position": v(84.37, 140.62) * mm});
            skPoint(sketch, "E343", {"position": v(103.12, 140.62) * mm});
            skPoint(sketch, "E344", {"position": v(121.87, 140.62) * mm});
            skPoint(sketch, "E345", {"position": v(140.62, 140.62) * mm});
            skPoint(sketch, "E346", {"position": v(159.37, 140.62) * mm});
            skPoint(sketch, "E347", {"position": v(178.12, 140.62) * mm});
            skPoint(sketch, "E348", {"position": v(196.87, 140.62) * mm});
            skPoint(sketch, "E349", {"position": v(215.62, 140.62) * mm});
            skPoint(sketch, "E350", {"position": v(234.37, 140.62) * mm});
            skPoint(sketch, "E351", {"position": v(253.12, 140.62) * mm});
            skPoint(sketch, "E352", {"position": v(271.87, 140.62) * mm});
            skPoint(sketch, "E353", {"position": v(28.12, 121.87) * mm});
            skPoint(sketch, "E354", {"position": v(46.87, 121.87) * mm});
            skPoint(sketch, "E355", {"position": v(65.62, 121.87) * mm});
            skPoint(sketch, "E356", {"position": v(84.37, 121.87) * mm});
            skPoint(sketch, "E357", {"position": v(103.12, 121.87) * mm});
            skPoint(sketch, "E358", {"position": v(121.87, 121.87) * mm});
            skPoint(sketch, "E359", {"position": v(140.62, 121.87) * mm});
            skPoint(sketch, "E360", {"position": v(159.37, 121.87) * mm});
            skPoint(sketch, "E361", {"position": v(178.12, 121.87) * mm});
            skPoint(sketch, "E362", {"position": v(196.87, 121.87) * mm});
            skPoint(sketch, "E363", {"position": v(215.62, 121.87) * mm});
            skPoint(sketch, "E364", {"position": v(234.37, 121.87) * mm});
            skPoint(sketch, "E365", {"position": v(253.12, 121.87) * mm});
            skPoint(sketch, "E366", {"position": v(271.87, 121.87) * mm});
            skPoint(sketch, "E367", {"position": v(-9.38, 103.12) * mm});
            skPoint(sketch, "E368", {"position": v(9.37, 103.12) * mm});
            skPoint(sketch, "E369", {"position": v(28.12, 103.12) * mm});
            skPoint(sketch, "E370", {"position": v(46.87, 103.12) * mm});
            skPoint(sketch, "E371", {"position": v(65.62, 103.12) * mm});
            skPoint(sketch, "E372", {"position": v(84.37, 103.12) * mm});
            skPoint(sketch, "E373", {"position": v(103.12, 103.12) * mm});
            skPoint(sketch, "E374", {"position": v(121.87, 103.12) * mm});
            skPoint(sketch, "E375", {"position": v(140.62, 103.12) * mm});
            skPoint(sketch, "E376", {"position": v(159.37, 103.12) * mm});
            skPoint(sketch, "E377", {"position": v(178.12, 103.12) * mm});
            skPoint(sketch, "E378", {"position": v(196.87, 103.12) * mm});
            skPoint(sketch, "E379", {"position": v(215.62, 103.12) * mm});
            skPoint(sketch, "E380", {"position": v(234.37, 103.12) * mm});
            skPoint(sketch, "E381", {"position": v(253.12, 103.12) * mm});
            skPoint(sketch, "E382", {"position": v(271.87, 103.12) * mm});
            skPoint(sketch, "E383", {"position": v(290.62, 103.12) * mm});
            skPoint(sketch, "E384", {"position": v(121.87, 84.37) * mm});
            skPoint(sketch, "E385", {"position": v(140.62, 84.37) * mm});
            skPoint(sketch, "E386", {"position": v(159.37, 84.37) * mm});
            skPoint(sketch, "E387", {"position": v(178.12, 84.37) * mm});
            skPoint(sketch, "E388", {"position": v(196.87, 84.37) * mm});
            skPoint(sketch, "E389", {"position": v(215.62, 84.37) * mm});
            skPoint(sketch, "E390", {"position": v(234.37, 84.37) * mm});
            skPoint(sketch, "E391", {"position": v(253.12, 84.37) * mm});
            skPoint(sketch, "E392", {"position": v(271.87, 84.37) * mm});
            skPoint(sketch, "E393", {"position": v(65.62, 65.62) * mm});
            skPoint(sketch, "E394", {"position": v(84.37, 65.62) * mm});
            skPoint(sketch, "E395", {"position": v(121.87, 65.62) * mm});
            skPoint(sketch, "E396", {"position": v(140.62, 65.62) * mm});
            skPoint(sketch, "E397", {"position": v(159.37, 65.62) * mm});
            skPoint(sketch, "E398", {"position": v(178.12, 65.62) * mm});
            skPoint(sketch, "E399", {"position": v(196.87, 65.62) * mm});
            skPoint(sketch, "E400", {"position": v(215.62, 65.62) * mm});
            skPoint(sketch, "E401", {"position": v(234.37, 65.62) * mm});
            skPoint(sketch, "E402", {"position": v(253.12, 65.62) * mm});
            skPoint(sketch, "E403", {"position": v(-28.13, 46.87) * mm});
            skPoint(sketch, "E404", {"position": v(-9.38, 46.87) * mm});
            skPoint(sketch, "E405", {"position": v(65.62, 46.87) * mm});
            skPoint(sketch, "E406", {"position": v(84.37, 46.87) * mm});
            skPoint(sketch, "E407", {"position": v(103.12, 46.87) * mm});
            skPoint(sketch, "E408", {"position": v(121.87, 46.87) * mm});
            skPoint(sketch, "E409", {"position": v(140.62, 46.87) * mm});
            skPoint(sketch, "E410", {"position": v(159.37, 46.87) * mm});
            skPoint(sketch, "E411", {"position": v(178.12, 46.87) * mm});
            skPoint(sketch, "E412", {"position": v(196.87, 46.87) * mm});
            skPoint(sketch, "E413", {"position": v(215.62, 46.87) * mm});
            skPoint(sketch, "E414", {"position": v(234.37, 46.87) * mm});
            skPoint(sketch, "E415", {"position": v(253.12, 46.87) * mm});
            skPoint(sketch, "E416", {"position": v(-46.88, 28.12) * mm});
            skPoint(sketch, "E417", {"position": v(-28.13, 28.12) * mm});
            skPoint(sketch, "E418", {"position": v(-9.38, 28.12) * mm});
            skPoint(sketch, "E419", {"position": v(9.37, 28.12) * mm});
            skPoint(sketch, "E420", {"position": v(28.12, 28.12) * mm});
            skPoint(sketch, "E421", {"position": v(46.87, 28.12) * mm});
            skPoint(sketch, "E422", {"position": v(84.37, 28.12) * mm});
            skPoint(sketch, "E423", {"position": v(84.37, 9.37) * mm});
            skPoint(sketch, "E424", {"position": v(103.12, 9.37) * mm});
            skPoint(sketch, "E425", {"position": v(159.37, 28.12) * mm});
            skPoint(sketch, "E426", {"position": v(178.12, 28.12) * mm});
            skPoint(sketch, "E427", {"position": v(196.87, 28.12) * mm});
            skPoint(sketch, "E428", {"position": v(215.62, 28.12) * mm});
            skPoint(sketch, "E429", {"position": v(234.37, 28.12) * mm});
            skPoint(sketch, "E430", {"position": v(253.12, 28.12) * mm});
            skPoint(sketch, "E431", {"position": v(234.37, 9.37) * mm});
            skPoint(sketch, "E432", {"position": v(178.12, 9.37) * mm});
            skPoint(sketch, "E433", {"position": v(-65.63, 9.37) * mm});
            skPoint(sketch, "E434", {"position": v(-46.88, 9.37) * mm});
            skPoint(sketch, "E435", {"position": v(-28.13, 9.37) * mm});
            skPoint(sketch, "E436", {"position": v(-9.38, 9.37) * mm});
            skPoint(sketch, "E437", {"position": v(9.37, 9.37) * mm});
            skPoint(sketch, "E438", {"position": v(28.12, 9.37) * mm});
            skPoint(sketch, "E439", {"position": v(46.87, 9.37) * mm});
            skPoint(sketch, "E440", {"position": v(-65.63, -9.38) * mm});
            skPoint(sketch, "E441", {"position": v(-46.88, -9.38) * mm});
            skPoint(sketch, "E442", {"position": v(-28.13, -9.38) * mm});
            skPoint(sketch, "E443", {"position": v(-9.38, -9.38) * mm});
            skPoint(sketch, "E444", {"position": v(9.37, -9.38) * mm});
            skPoint(sketch, "E445", {"position": v(28.12, -9.38) * mm});
            skPoint(sketch, "E446", {"position": v(46.87, -9.38) * mm});
            skPoint(sketch, "E447", {"position": v(65.62, -9.38) * mm});
            skPoint(sketch, "E448", {"position": v(-46.88, -28.13) * mm});
            skPoint(sketch, "E449", {"position": v(-28.13, -28.13) * mm});
            skPoint(sketch, "E450", {"position": v(-9.38, -28.13) * mm});
            skPoint(sketch, "E451", {"position": v(9.37, -28.13) * mm});
            skPoint(sketch, "E452", {"position": v(28.12, -28.13) * mm});
            skPoint(sketch, "E453", {"position": v(46.87, -28.13) * mm});
            skPoint(sketch, "E454", {"position": v(65.62, -28.13) * mm});
            skPoint(sketch, "E455", {"position": v(84.37, -28.13) * mm});
            skPoint(sketch, "E456", {"position": v(9.37, -46.88) * mm});
            skPoint(sketch, "E457", {"position": v(28.12, -46.88) * mm});
            skPoint(sketch, "E458", {"position": v(46.87, -46.88) * mm});
            skPoint(sketch, "E459", {"position": v(65.62, -46.88) * mm});
            skPoint(sketch, "E460", {"position": v(9.37, -65.63) * mm});
            skPoint(sketch, "E461", {"position": v(28.12, -65.63) * mm});
            skPoint(sketch, "E462", {"position": v(46.87, -65.63) * mm});
            skPoint(sketch, "E463", {"position": v(65.62, -65.63) * mm});
            skPoint(sketch, "E464", {"position": v(28.12, -84.38) * mm});
            skPoint(sketch, "E465", {"position": v(46.87, -84.38) * mm});
            skPoint(sketch, "E466", {"position": v(65.62, -84.38) * mm});
            skPoint(sketch, "E467", {"position": v(28.12, -103.13) * mm});
            skPoint(sketch, "E468", {"position": v(46.87, -103.13) * mm});
            skPoint(sketch, "E469", {"position": v(65.62, -103.13) * mm});
            skPoint(sketch, "E470", {"position": v(28.12, -121.88) * mm});
            skPoint(sketch, "E471", {"position": v(46.87, -121.88) * mm});
            skPoint(sketch, "E472", {"position": v(28.12, -140.63) * mm});
            skPoint(sketch, "E473", {"position": v(271.87, -140.63) * mm});
            skPoint(sketch, "E474", {"position": v(290.62, -121.88) * mm});
            skPoint(sketch, "E475", {"position": v(309.37, -121.88) * mm});
            skPoint(sketch, "E476", {"position": v(328.12, -121.88) * mm});
            skPoint(sketch, "E477", {"position": v(290.62, -140.63) * mm});
            skPoint(sketch, "E478", {"position": v(309.37, -140.63) * mm});
            skPoint(sketch, "E479", {"position": v(328.12, -140.63) * mm});
            skPoint(sketch, "E480", {"position": v(328.12, -159.38) * mm});
            skPoint(sketch, "E481", {"position": v(346.87, -140.63) * mm});
            skSolve(sketch);
        }
        {
            var Q0;
            Q0=sQuery(id+"F10.wireOp",VERTEX,"E360");
            var Q1;
            Q1=sQuery(id+"F10.wireOp",VERTEX,"E348");
            var Q2;
            Q2=sQuery(id+"F10.wireOp",VERTEX,"E359");
            var Q3;
            Q3=sQuery(id+"F10.wireOp",VERTEX,"E329");
            var Q4;
            Q4=sQuery(id+"F10.wireOp",VERTEX,"E365");
            var Q5;
            Q5=sQuery(id+"F10.wireOp",VERTEX,"E414");
            var Q6;
            Q6=sQuery(id+"F10.wireOp",VERTEX,"E363");
            var Q7;
            Q7=sQuery(id+"F10.wireOp",VERTEX,"E347");
            var Q8;
            Q8=sQuery(id+"F10.wireOp",VERTEX,"E429");
            var Q9;
            Q9=sQuery(id+"F10.wireOp",VERTEX,"E333");
            var Q10;
            Q10=sQuery(id+"F10.wireOp",VERTEX,"E409");
            var Q11;
            Q11=sQuery(id+"F10.wireOp",VERTEX,"E331");
            var Q12;
            Q12=sQuery(id+"F10.wireOp",VERTEX,"E474");
            var Q13;
            Q13=sQuery(id+"F10.wireOp",VERTEX,"E410");
            var Q14;
            Q14=sQuery(id+"F10.wireOp",VERTEX,"E392");
            var Q15;
            Q15=sQuery(id+"F10.wireOp",VERTEX,"E346");
            var Q16;
            Q16=sQuery(id+"F10.wireOp",VERTEX,"E378");
            var Q17;
            Q17=sQuery(id+"F10.wireOp",VERTEX,"E362");
            var Q18;
            Q18=sQuery(id+"F10.wireOp",VERTEX,"E388");
            var Q19;
            Q19=sQuery(id+"F10.wireOp",VERTEX,"E476");
            var Q20;
            Q20=sQuery(id+"F10.wireOp",VERTEX,"E411");
            var Q21;
            Q21=sQuery(id+"F10.wireOp",VERTEX,"E479");
            var Q22;
            Q22=sQuery(id+"F10.wireOp",VERTEX,"E379");
            var Q23;
            Q23=sQuery(id+"F10.wireOp",VERTEX,"E389");
            var Q24;
            Q24=sQuery(id+"F10.wireOp",VERTEX,"E397");
            var Q25;
            Q25=sQuery(id+"F10.wireOp",VERTEX,"E400");
            var Q26;
            Q26=sQuery(id+"F10.wireOp",VERTEX,"E428");
            var Q27;
            Q27=sQuery(id+"F10.wireOp",VERTEX,"E385");
            var Q28;
            Q28=sQuery(id+"F10.wireOp",VERTEX,"E430");
            var Q29;
            Q29=sQuery(id+"F10.wireOp",VERTEX,"E345");
            var Q30;
            Q30=sQuery(id+"F10.wireOp",VERTEX,"E351");
            var Q31;
            Q31=sQuery(id+"F10.wireOp",VERTEX,"E337");
            var Q32;
            Q32=sQuery(id+"F10.wireOp",VERTEX,"E475");
            var Q33;
            Q33=sQuery(id+"F10.wireOp",VERTEX,"E391");
            var Q34;
            Q34=sQuery(id+"F10.wireOp",VERTEX,"E402");
            var Q35;
            Q35=sQuery(id+"F10.wireOp",VERTEX,"E335");
            var Q36;
            Q36=sQuery(id+"F10.wireOp",VERTEX,"E427");
            var Q37;
            Q37=sQuery(id+"F10.wireOp",VERTEX,"E413");
            var Q38;
            Q38=sQuery(id+"F10.wireOp",VERTEX,"E396");
            var Q39;
            Q39=sQuery(id+"F10.wireOp",VERTEX,"E366");
            var Q40;
            Q40=sQuery(id+"F10.wireOp",VERTEX,"E330");
            var Q41;
            Q41=sQuery(id+"F10.wireOp",VERTEX,"E349");
            var Q42;
            Q42=sQuery(id+"F10.wireOp",VERTEX,"E381");
            var Q43;
            Q43=sQuery(id+"F10.wireOp",VERTEX,"E376");
            var Q44;
            Q44=sQuery(id+"F10.wireOp",VERTEX,"E380");
            var Q45;
            Q45=sQuery(id+"F10.wireOp",VERTEX,"E375");
            var Q46;
            Q46=sQuery(id+"F10.wireOp",VERTEX,"E432");
            var Q47;
            Q47=sQuery(id+"F10.wireOp",VERTEX,"E390");
            var Q48;
            Q48=sQuery(id+"F10.wireOp",VERTEX,"E332");
            var Q49;
            Q49=sQuery(id+"F10.wireOp",VERTEX,"E339");
            var Q50;
            Q50=sQuery(id+"F10.wireOp",VERTEX,"E383");
            var Q51;
            Q51=sQuery(id+"F10.wireOp",VERTEX,"E386");
            var Q52;
            Q52=sQuery(id+"F10.wireOp",VERTEX,"E415");
            var Q53;
            Q53=sQuery(id+"F10.wireOp",VERTEX,"E426");
            var Q54;
            Q54=sQuery(id+"F10.wireOp",VERTEX,"E481");
            var Q55;
            Q55=sQuery(id+"F10.wireOp",VERTEX,"E364");
            var Q56;
            Q56=sQuery(id+"F10.wireOp",VERTEX,"E350");
            var Q57;
            Q57=sQuery(id+"F10.wireOp",VERTEX,"E328");
            var Q58;
            Q58=sQuery(id+"F10.wireOp",VERTEX,"E399");
            var Q59;
            Q59=sQuery(id+"F10.wireOp",VERTEX,"E431");
            var Q60;
            Q60=sQuery(id+"F10.wireOp",VERTEX,"E473");
            var Q61;
            Q61=sQuery(id+"F10.wireOp",VERTEX,"E382");
            var Q62;
            Q62=sQuery(id+"F10.wireOp",VERTEX,"E352");
            var Q63;
            Q63=sQuery(id+"F10.wireOp",VERTEX,"E338");
            var Q64;
            Q64=sQuery(id+"F10.wireOp",VERTEX,"E401");
            var Q65;
            Q65=sQuery(id+"F10.wireOp",VERTEX,"E336");
            var Q66;
            Q66=sQuery(id+"F10.wireOp",VERTEX,"E398");
            var Q67;
            Q67=sQuery(id+"F10.wireOp",VERTEX,"E377");
            var Q68;
            Q68=sQuery(id+"F10.wireOp",VERTEX,"E480");
            var Q69;
            Q69=sQuery(id+"F10.wireOp",VERTEX,"E334");
            var Q70;
            Q70=sQuery(id+"F10.wireOp",VERTEX,"E412");
            var Q71;
            Q71=sQuery(id+"F10.wireOp",VERTEX,"E361");
            var Q72;
            Q72=sQuery(id+"F10.wireOp",VERTEX,"E478");
            var Q73;
            Q73=sQuery(id+"F10.wireOp",VERTEX,"E425");
            var Q74;
            Q74=sQuery(id+"F10.wireOp",VERTEX,"E387");
            var Q75;
            Q75=sQuery(id+"F10.wireOp",VERTEX,"E477");
            var Q76;
            Q76=makeQuery(id+"F1.opExtrude","SWEPT_BODY",BODY,{"disambiguationData":[OSD([sQuery(id+"F0.wireOp",EDGE,"E0.bottom"),sQuery(id+"F0.wireOp",EDGE,"E0.top"),sQuery(id+"F0.wireOp",EDGE,"E0.left"),sQuery(id+"F0.wireOp",EDGE,"E0.right")])]});
            hole(context, id + "F11", {"style" : HoleStyle.SIMPLE, "endStyle" : HoleEndStyle.THROUGH, "holeDiameter" : 10 * mm, "isTappedThrough" : true, "tappedDepth" : 12 * mm, "tapClearance" : 3, "locations" : qUnion([Q0, Q1, Q2, Q3, Q4, Q5, Q6, Q7, Q8, Q9, Q10, Q11, Q12, Q13, Q14, Q15, Q16, Q17, Q18, Q19, Q20, Q21, Q22, Q23, Q24, Q25, Q26, Q27, Q28, Q29, Q30, Q31, Q32, Q33, Q34, Q35, Q36, Q37, Q38, Q39, Q40, Q41, Q42, Q43, Q44, Q45, Q46, Q47, Q48, Q49, Q50, Q51, Q52, Q53, Q54, Q55, Q56, Q57, Q58, Q59, Q60, Q61, Q62, Q63, Q64, Q65, Q66, Q67, Q68, Q69, Q70, Q71, Q72, Q73, Q74, Q75]), "scope" : qUnion([Q76])});
        }
        {
            var Q0;
            Q0=sQuery(id+"F10.wireOp",VERTEX,"E371");
            var Q1;
            Q1=sQuery(id+"F10.wireOp",VERTEX,"E373");
            var Q2;
            Q2=sQuery(id+"F10.wireOp",VERTEX,"E320");
            var Q3;
            Q3=sQuery(id+"F10.wireOp",VERTEX,"E340");
            var Q4;
            Q4=sQuery(id+"F10.wireOp",VERTEX,"E343");
            var Q5;
            Q5=sQuery(id+"F10.wireOp",VERTEX,"E420");
            var Q6;
            Q6=sQuery(id+"F10.wireOp",VERTEX,"E358");
            var Q7;
            Q7=sQuery(id+"F10.wireOp",VERTEX,"E341");
            var Q8;
            Q8=sQuery(id+"F10.wireOp",VERTEX,"E448");
            var Q9;
            Q9=sQuery(id+"F10.wireOp",VERTEX,"E455");
            var Q10;
            Q10=sQuery(id+"F10.wireOp",VERTEX,"E326");
            var Q11;
            Q11=sQuery(id+"F10.wireOp",VERTEX,"E355");
            var Q12;
            Q12=sQuery(id+"F10.wireOp",VERTEX,"E436");
            var Q13;
            Q13=sQuery(id+"F10.wireOp",VERTEX,"E472");
            var Q14;
            Q14=sQuery(id+"F10.wireOp",VERTEX,"E407");
            var Q15;
            Q15=sQuery(id+"F10.wireOp",VERTEX,"E259");
            var Q16;
            Q16=sQuery(id+"F10.wireOp",VERTEX,"E264");
            var Q17;
            Q17=sQuery(id+"F10.wireOp",VERTEX,"E405");
            var Q18;
            Q18=sQuery(id+"F10.wireOp",VERTEX,"E452");
            var Q19;
            Q19=sQuery(id+"F10.wireOp",VERTEX,"E395");
            var Q20;
            Q20=sQuery(id+"F10.wireOp",VERTEX,"E443");
            var Q21;
            Q21=sQuery(id+"F10.wireOp",VERTEX,"E318");
            var Q22;
            Q22=sQuery(id+"F10.wireOp",VERTEX,"E369");
            var Q23;
            Q23=sQuery(id+"F10.wireOp",VERTEX,"E319");
            var Q24;
            Q24=sQuery(id+"F10.wireOp",VERTEX,"E461");
            var Q25;
            Q25=sQuery(id+"F10.wireOp",VERTEX,"E437");
            var Q26;
            Q26=sQuery(id+"F10.wireOp",VERTEX,"E327");
            var Q27;
            Q27=sQuery(id+"F10.wireOp",VERTEX,"E423");
            var Q28;
            Q28=sQuery(id+"F10.wireOp",VERTEX,"E354");
            var Q29;
            Q29=sQuery(id+"F10.wireOp",VERTEX,"E325");
            var Q30;
            Q30=sQuery(id+"F10.wireOp",VERTEX,"E469");
            var Q31;
            Q31=sQuery(id+"F10.wireOp",VERTEX,"E441");
            var Q32;
            Q32=sQuery(id+"F10.wireOp",VERTEX,"E444");
            var Q33;
            Q33=sQuery(id+"F10.wireOp",VERTEX,"E374");
            var Q34;
            Q34=sQuery(id+"F10.wireOp",VERTEX,"E317");
            var Q35;
            Q35=sQuery(id+"F10.wireOp",VERTEX,"E445");
            var Q36;
            Q36=sQuery(id+"F10.wireOp",VERTEX,"E424");
            var Q37;
            Q37=sQuery(id+"F10.wireOp",VERTEX,"E447");
            var Q38;
            Q38=sQuery(id+"F10.wireOp",VERTEX,"E418");
            var Q39;
            Q39=sQuery(id+"F10.wireOp",VERTEX,"E416");
            var Q40;
            Q40=sQuery(id+"F10.wireOp",VERTEX,"E451");
            var Q41;
            Q41=sQuery(id+"F10.wireOp",VERTEX,"E471");
            var Q42;
            Q42=sQuery(id+"F10.wireOp",VERTEX,"E263");
            var Q43;
            Q43=sQuery(id+"F10.wireOp",VERTEX,"E342");
            var Q44;
            Q44=sQuery(id+"F10.wireOp",VERTEX,"E438");
            var Q45;
            Q45=sQuery(id+"F10.wireOp",VERTEX,"E344");
            var Q46;
            Q46=sQuery(id+"F10.wireOp",VERTEX,"E456");
            var Q47;
            Q47=sQuery(id+"F10.wireOp",VERTEX,"E465");
            var Q48;
            Q48=sQuery(id+"F10.wireOp",VERTEX,"E404");
            var Q49;
            Q49=sQuery(id+"F10.wireOp",VERTEX,"E356");
            var Q50;
            Q50=sQuery(id+"F10.wireOp",VERTEX,"E384");
            var Q51;
            Q51=sQuery(id+"F10.wireOp",VERTEX,"E468");
            var Q52;
            Q52=sQuery(id+"F10.wireOp",VERTEX,"E419");
            var Q53;
            Q53=sQuery(id+"F10.wireOp",VERTEX,"E262");
            var Q54;
            Q54=sQuery(id+"F10.wireOp",VERTEX,"E439");
            var Q55;
            Q55=sQuery(id+"F10.wireOp",VERTEX,"E463");
            var Q56;
            Q56=sQuery(id+"F10.wireOp",VERTEX,"E367");
            var Q57;
            Q57=sQuery(id+"F10.wireOp",VERTEX,"E454");
            var Q58;
            Q58=sQuery(id+"F10.wireOp",VERTEX,"E422");
            var Q59;
            Q59=sQuery(id+"F10.wireOp",VERTEX,"E435");
            var Q60;
            Q60=sQuery(id+"F10.wireOp",VERTEX,"E368");
            var Q61;
            Q61=sQuery(id+"F10.wireOp",VERTEX,"E433");
            var Q62;
            Q62=sQuery(id+"F10.wireOp",VERTEX,"E417");
            var Q63;
            Q63=sQuery(id+"F10.wireOp",VERTEX,"E470");
            var Q64;
            Q64=sQuery(id+"F10.wireOp",VERTEX,"E459");
            var Q65;
            Q65=sQuery(id+"F10.wireOp",VERTEX,"E434");
            var Q66;
            Q66=sQuery(id+"F10.wireOp",VERTEX,"E408");
            var Q67;
            Q67=sQuery(id+"F10.wireOp",VERTEX,"E406");
            var Q68;
            Q68=sQuery(id+"F10.wireOp",VERTEX,"E458");
            var Q69;
            Q69=sQuery(id+"F10.wireOp",VERTEX,"E394");
            var Q70;
            Q70=sQuery(id+"F10.wireOp",VERTEX,"E353");
            var Q71;
            Q71=sQuery(id+"F10.wireOp",VERTEX,"E453");
            var Q72;
            Q72=sQuery(id+"F10.wireOp",VERTEX,"E357");
            var Q73;
            Q73=sQuery(id+"F10.wireOp",VERTEX,"E457");
            var Q74;
            Q74=sQuery(id+"F10.wireOp",VERTEX,"E450");
            var Q75;
            Q75=sQuery(id+"F10.wireOp",VERTEX,"E393");
            var Q76;
            Q76=sQuery(id+"F10.wireOp",VERTEX,"E464");
            var Q77;
            Q77=sQuery(id+"F10.wireOp",VERTEX,"E449");
            var Q78;
            Q78=sQuery(id+"F10.wireOp",VERTEX,"E462");
            var Q79;
            Q79=sQuery(id+"F10.wireOp",VERTEX,"E372");
            var Q80;
            Q80=sQuery(id+"F10.wireOp",VERTEX,"E466");
            var Q81;
            Q81=sQuery(id+"F10.wireOp",VERTEX,"E260");
            var Q82;
            Q82=sQuery(id+"F10.wireOp",VERTEX,"E467");
            var Q83;
            Q83=sQuery(id+"F10.wireOp",VERTEX,"E261");
            var Q84;
            Q84=sQuery(id+"F10.wireOp",VERTEX,"E460");
            var Q85;
            Q85=sQuery(id+"F10.wireOp",VERTEX,"E421");
            var Q86;
            Q86=sQuery(id+"F10.wireOp",VERTEX,"E440");
            var Q87;
            Q87=sQuery(id+"F10.wireOp",VERTEX,"E370");
            var Q88;
            Q88=sQuery(id+"F10.wireOp",VERTEX,"E446");
            var Q89;
            Q89=sQuery(id+"F10.wireOp",VERTEX,"E403");
            var Q90;
            Q90=sQuery(id+"F10.wireOp",VERTEX,"E442");
            var Q91;
            Q91=makeQuery(id+"F1.opExtrude","SWEPT_BODY",BODY,{"disambiguationData":[OSD([sQuery(id+"F0.wireOp",EDGE,"E0.bottom"),sQuery(id+"F0.wireOp",EDGE,"E0.top"),sQuery(id+"F0.wireOp",EDGE,"E0.left"),sQuery(id+"F0.wireOp",EDGE,"E0.right")])]});
            hole(context, id + "F12", {"style" : HoleStyle.SIMPLE, "endStyle" : HoleEndStyle.THROUGH, "holeDiameter" : 10 * mm, "isTappedThrough" : true, "tappedDepth" : 12 * mm, "tapClearance" : 3, "locations" : qUnion([Q0, Q1, Q2, Q3, Q4, Q5, Q6, Q7, Q8, Q9, Q10, Q11, Q12, Q13, Q14, Q15, Q16, Q17, Q18, Q19, Q20, Q21, Q22, Q23, Q24, Q25, Q26, Q27, Q28, Q29, Q30, Q31, Q32, Q33, Q34, Q35, Q36, Q37, Q38, Q39, Q40, Q41, Q42, Q43, Q44, Q45, Q46, Q47, Q48, Q49, Q50, Q51, Q52, Q53, Q54, Q55, Q56, Q57, Q58, Q59, Q60, Q61, Q62, Q63, Q64, Q65, Q66, Q67, Q68, Q69, Q70, Q71, Q72, Q73, Q74, Q75, Q76, Q77, Q78, Q79, Q80, Q81, Q82, Q83, Q84, Q85, Q86, Q87, Q88, Q89, Q90]), "scope" : qUnion([Q91])});
        }
        {
            var Q0;
            Q0=sQuery(id+"F10.wireOp",VERTEX,"E308");
            var Q1;
            Q1=sQuery(id+"F10.wireOp",VERTEX,"E300");
            var Q2;
            Q2=sQuery(id+"F10.wireOp",VERTEX,"E306");
            var Q3;
            Q3=sQuery(id+"F10.wireOp",VERTEX,"E310");
            var Q4;
            Q4=sQuery(id+"F10.wireOp",VERTEX,"E297");
            var Q5;
            Q5=sQuery(id+"F10.wireOp",VERTEX,"E303");
            var Q6;
            Q6=sQuery(id+"F10.wireOp",VERTEX,"E315");
            var Q7;
            Q7=sQuery(id+"F10.wireOp",VERTEX,"E272");
            var Q8;
            Q8=sQuery(id+"F10.wireOp",VERTEX,"E269");
            var Q9;
            Q9=sQuery(id+"F10.wireOp",VERTEX,"E313");
            var Q10;
            Q10=sQuery(id+"F10.wireOp",VERTEX,"E265");
            var Q11;
            Q11=sQuery(id+"F10.wireOp",VERTEX,"E276");
            var Q12;
            Q12=sQuery(id+"F10.wireOp",VERTEX,"E266");
            var Q13;
            Q13=sQuery(id+"F10.wireOp",VERTEX,"E298");
            var Q14;
            Q14=sQuery(id+"F10.wireOp",VERTEX,"E296");
            var Q15;
            Q15=sQuery(id+"F10.wireOp",VERTEX,"E280");
            var Q16;
            Q16=sQuery(id+"F10.wireOp",VERTEX,"E290");
            var Q17;
            Q17=sQuery(id+"F10.wireOp",VERTEX,"E286");
            var Q18;
            Q18=sQuery(id+"F10.wireOp",VERTEX,"E302");
            var Q19;
            Q19=sQuery(id+"F10.wireOp",VERTEX,"E278");
            var Q20;
            Q20=sQuery(id+"F10.wireOp",VERTEX,"E322");
            var Q21;
            Q21=sQuery(id+"F10.wireOp",VERTEX,"E285");
            var Q22;
            Q22=sQuery(id+"F10.wireOp",VERTEX,"E287");
            var Q23;
            Q23=sQuery(id+"F10.wireOp",VERTEX,"E312");
            var Q24;
            Q24=sQuery(id+"F10.wireOp",VERTEX,"E274");
            var Q25;
            Q25=sQuery(id+"F10.wireOp",VERTEX,"E301");
            var Q26;
            Q26=sQuery(id+"F10.wireOp",VERTEX,"E311");
            var Q27;
            Q27=sQuery(id+"F10.wireOp",VERTEX,"E321");
            var Q28;
            Q28=sQuery(id+"F10.wireOp",VERTEX,"E316");
            var Q29;
            Q29=sQuery(id+"F10.wireOp",VERTEX,"E309");
            var Q30;
            Q30=sQuery(id+"F10.wireOp",VERTEX,"E270");
            var Q31;
            Q31=sQuery(id+"F10.wireOp",VERTEX,"E307");
            var Q32;
            Q32=sQuery(id+"F10.wireOp",VERTEX,"E291");
            var Q33;
            Q33=sQuery(id+"F10.wireOp",VERTEX,"E273");
            var Q34;
            Q34=sQuery(id+"F10.wireOp",VERTEX,"E324");
            var Q35;
            Q35=sQuery(id+"F10.wireOp",VERTEX,"E299");
            var Q36;
            Q36=sQuery(id+"F10.wireOp",VERTEX,"E283");
            var Q37;
            Q37=sQuery(id+"F10.wireOp",VERTEX,"E305");
            var Q38;
            Q38=sQuery(id+"F10.wireOp",VERTEX,"E282");
            var Q39;
            Q39=sQuery(id+"F10.wireOp",VERTEX,"E268");
            var Q40;
            Q40=sQuery(id+"F10.wireOp",VERTEX,"E275");
            var Q41;
            Q41=sQuery(id+"F10.wireOp",VERTEX,"E281");
            var Q42;
            Q42=sQuery(id+"F10.wireOp",VERTEX,"E294");
            var Q43;
            Q43=sQuery(id+"F10.wireOp",VERTEX,"E323");
            var Q44;
            Q44=sQuery(id+"F10.wireOp",VERTEX,"E279");
            var Q45;
            Q45=sQuery(id+"F10.wireOp",VERTEX,"E284");
            var Q46;
            Q46=sQuery(id+"F10.wireOp",VERTEX,"E292");
            var Q47;
            Q47=sQuery(id+"F10.wireOp",VERTEX,"E271");
            var Q48;
            Q48=sQuery(id+"F10.wireOp",VERTEX,"E289");
            var Q49;
            Q49=sQuery(id+"F10.wireOp",VERTEX,"E267");
            var Q50;
            Q50=sQuery(id+"F10.wireOp",VERTEX,"E314");
            var Q51;
            Q51=sQuery(id+"F10.wireOp",VERTEX,"E277");
            var Q52;
            Q52=sQuery(id+"F10.wireOp",VERTEX,"E293");
            var Q53;
            Q53=sQuery(id+"F10.wireOp",VERTEX,"E304");
            var Q54;
            Q54=sQuery(id+"F10.wireOp",VERTEX,"E295");
            var Q55;
            Q55=sQuery(id+"F10.wireOp",VERTEX,"E288");
            var Q56;
            Q56=makeQuery(id+"F1.opExtrude","SWEPT_BODY",BODY,{"disambiguationData":[OSD([sQuery(id+"F0.wireOp",EDGE,"E0.bottom"),sQuery(id+"F0.wireOp",EDGE,"E0.top"),sQuery(id+"F0.wireOp",EDGE,"E0.left"),sQuery(id+"F0.wireOp",EDGE,"E0.right")])]});
            hole(context, id + "F13", {"style" : HoleStyle.SIMPLE, "endStyle" : HoleEndStyle.THROUGH, "holeDiameter" : 10 * mm, "isTappedThrough" : true, "tappedDepth" : 12 * mm, "tapClearance" : 3, "locations" : qUnion([Q0, Q1, Q2, Q3, Q4, Q5, Q6, Q7, Q8, Q9, Q10, Q11, Q12, Q13, Q14, Q15, Q16, Q17, Q18, Q19, Q20, Q21, Q22, Q23, Q24, Q25, Q26, Q27, Q28, Q29, Q30, Q31, Q32, Q33, Q34, Q35, Q36, Q37, Q38, Q39, Q40, Q41, Q42, Q43, Q44, Q45, Q46, Q47, Q48, Q49, Q50, Q51, Q52, Q53, Q54, Q55]), "scope" : qUnion([Q56])});
        }
    });
